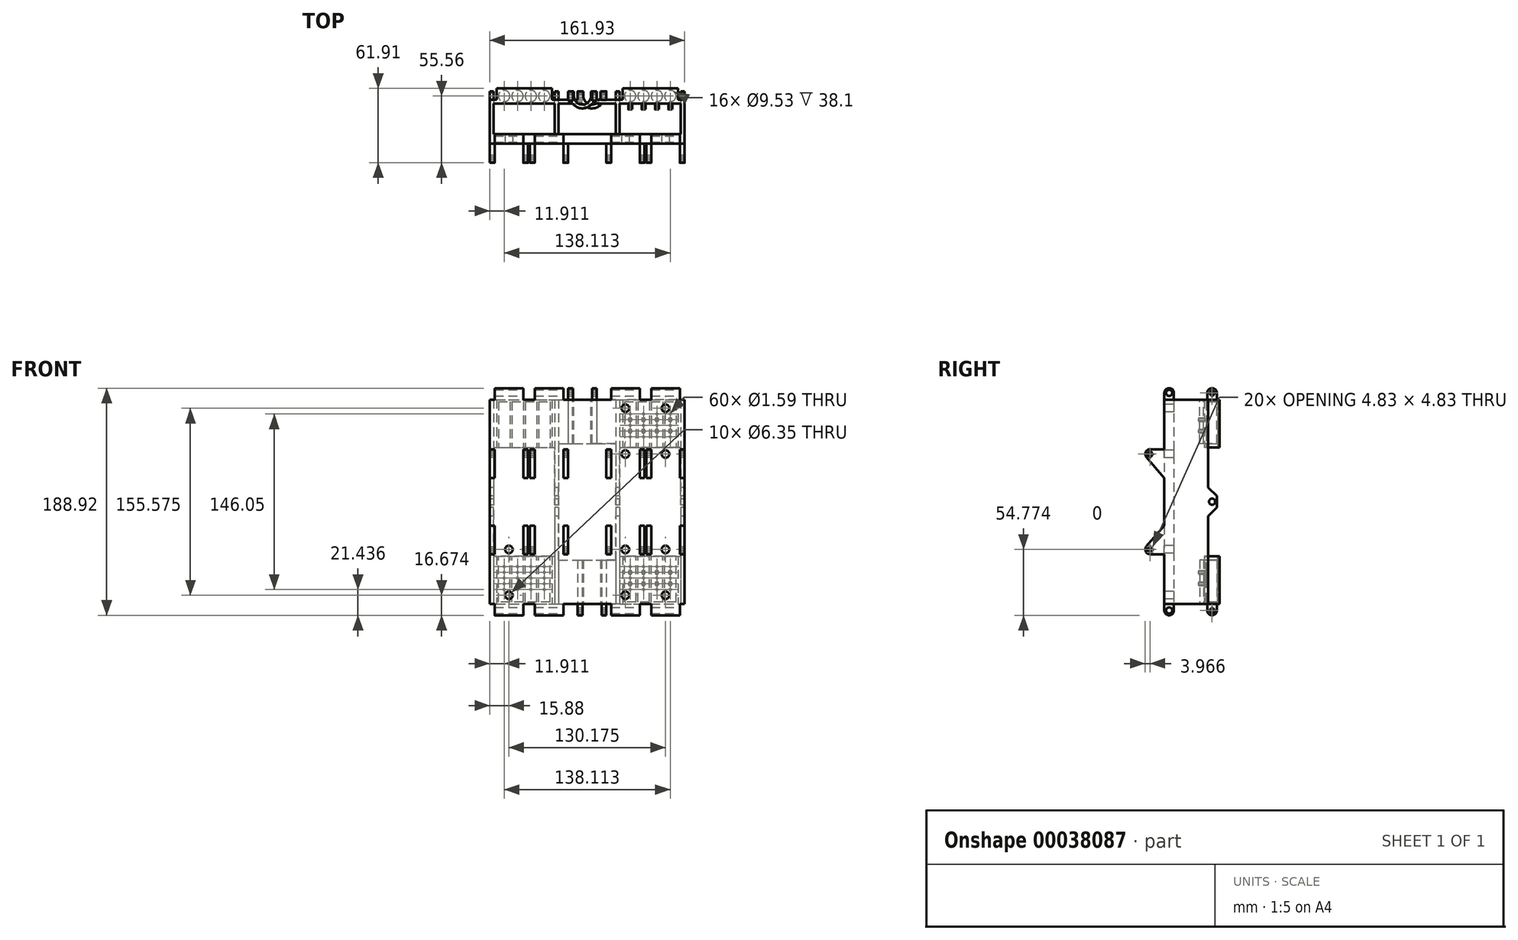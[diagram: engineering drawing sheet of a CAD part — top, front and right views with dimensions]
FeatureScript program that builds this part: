
annotation { "Feature Type Name" : "Feature", "Feature Type Description" : "" }
export const myFeature = defineFeature(function(context is Context, id is Id, definition is map)
    precondition{}
    {
        {
            var Q0;
            Q0=qCreatedBy(makeId("Top.planeOp"),FACE);
            var sketch = newSketch(context, id + "F0", { "sketchPlane" : qUnion([Q0])});
            skLineSegment(sketch, "E0.top", {"start": v(-3.18, -7.94) * mm, "end": v(158.75, -7.94) * mm});
            skLineSegment(sketch, "E1.left", {"start": v(0, 0) * mm, "end": v(0, 25.4) * mm});
            skLineSegment(sketch, "E1.right", {"start": v(-3.18, -7.94) * mm, "end": v(-3.17, 28.58) * mm});
            skLineSegment(sketch, "E2", {"start": v(0, 12.7) * mm, "end": v(-3.18, 12.7) * mm, "construction": true});
            skLineSegment(sketch, "E3", {"start": v(0, 0) * mm, "end": v(0, -7.94) * mm, "construction": true});
            skLineSegment(sketch, "E4.top", {"start": v(2.38, 38.1) * mm, "end": v(48.42, 38.1) * mm});
            skLineSegment(sketch, "E5.right", {"start": v(48.42, 28.57) * mm, "end": v(48.42, 38.1) * mm});
            skLineSegment(sketch, "E6", {"start": v(48.42, 28.57) * mm, "end": v(69.85, 28.57) * mm});
            skLineSegment(sketch, "E7.top", {"start": v(69.85, 35.72) * mm, "end": v(93.66, 35.72) * mm});
            skLineSegment(sketch, "E7.left", {"start": v(69.85, 28.57) * mm, "end": v(69.85, 35.72) * mm});
            skLineSegment(sketch, "E7.right", {"start": v(93.66, 28.57) * mm, "end": v(93.66, 35.72) * mm});
            skLineSegment(sketch, "E8.left", {"start": v(107.16, 28.57) * mm, "end": v(107.16, 38.1) * mm});
            skLineSegment(sketch, "E9", {"start": v(93.66, 28.57) * mm, "end": v(107.16, 28.57) * mm});
            skLineSegment(sketch, "E10.top", {"start": v(107.16, 38.1) * mm, "end": v(153.2, 38.1) * mm});
            skLineSegment(sketch, "E11", {"start": v(158.75, 28.57) * mm, "end": v(158.75, -7.94) * mm});
            skLineSegment(sketch, "E12", {"start": v(155.58, 25.4) * mm, "end": v(155.58, 0) * mm});
            skLineSegment(sketch, "E13", {"start": v(155.58, 12.7) * mm, "end": v(158.75, 12.7) * mm, "construction": true});
            skLineSegment(sketch, "E14", {"start": v(2.38, 38.1) * mm, "end": v(2.38, 28.57) * mm});
            skLineSegment(sketch, "E15", {"start": v(2.38, 28.58) * mm, "end": v(-3.18, 28.58) * mm});
            skLineSegment(sketch, "E16", {"start": v(153.2, 38.1) * mm, "end": v(153.2, 28.57) * mm});
            skLineSegment(sketch, "E17", {"start": v(153.2, 28.57) * mm, "end": v(158.75, 28.57) * mm});
            skLineSegment(sketch, "E18", {"start": v(0, 25.4) * mm, "end": v(50.8, 25.4) * mm});
            skLineSegment(sketch, "E19", {"start": v(0, 0) * mm, "end": v(50.8, 0) * mm});
            skLineSegment(sketch, "E20.bottom", {"start": v(50.8, 25.4) * mm, "end": v(53.98, 25.4) * mm, "construction": true});
            skLineSegment(sketch, "E20.top", {"start": v(50.8, 0) * mm, "end": v(53.98, 0) * mm, "construction": true});
            skLineSegment(sketch, "E20.left", {"start": v(50.8, 25.4) * mm, "end": v(50.8, 0) * mm});
            skLineSegment(sketch, "E20.right", {"start": v(53.98, 25.4) * mm, "end": v(53.98, 0) * mm});
            skLineSegment(sketch, "E21", {"start": v(53.98, 0) * mm, "end": v(101.6, 0) * mm});
            skLineSegment(sketch, "E22.bottom", {"start": v(101.6, 25.4) * mm, "end": v(104.78, 25.4) * mm, "construction": true});
            skLineSegment(sketch, "E22.top", {"start": v(101.6, 0) * mm, "end": v(104.78, 0) * mm, "construction": true});
            skLineSegment(sketch, "E22.left", {"start": v(101.6, 25.4) * mm, "end": v(101.6, 0) * mm});
            skLineSegment(sketch, "E22.right", {"start": v(104.78, 25.4) * mm, "end": v(104.78, 0) * mm});
            skLineSegment(sketch, "E23", {"start": v(104.78, 25.4) * mm, "end": v(155.58, 25.4) * mm});
            skLineSegment(sketch, "E24", {"start": v(104.78, 0) * mm, "end": v(155.58, 0) * mm});
            skLineSegment(sketch, "E25", {"start": v(0, 12.7) * mm, "end": v(25.4, 12.7) * mm, "construction": true});
            skLineSegment(sketch, "E26", {"start": v(25.4, 12.7) * mm, "end": v(25.4, 38.1) * mm, "construction": true});
            skLineSegment(sketch, "E27", {"start": v(155.58, 12.7) * mm, "end": v(104.78, 12.7) * mm, "construction": true});
            skLineSegment(sketch, "E28", {"start": v(53.98, 25.4) * mm, "end": v(69.85, 25.4) * mm});
            skLineSegment(sketch, "E29", {"start": v(101.6, 25.4) * mm, "end": v(93.66, 25.4) * mm});
            skLineSegment(sketch, "E30.top", {"start": v(69.85, 11.68) * mm, "end": v(93.66, 11.68) * mm});
            skLineSegment(sketch, "E30.left", {"start": v(69.85, 25.4) * mm, "end": v(69.85, 11.68) * mm});
            skLineSegment(sketch, "E30.right", {"start": v(93.66, 25.4) * mm, "end": v(93.66, 11.68) * mm});
            skLineSegment(sketch, "E31", {"start": v(25.4, 12.7) * mm, "end": v(50.8, 12.7) * mm, "construction": true});
            skLineSegment(sketch, "E32", {"start": v(81.76, 11.68) * mm, "end": v(81.76, 5.84) * mm, "construction": true});
            skLineSegment(sketch, "E33", {"start": v(81.76, 5.84) * mm, "end": v(77.79, 5.84) * mm, "construction": true});
            skLineSegment(sketch, "E34", {"start": v(77.79, 5.84) * mm, "end": v(77.79, 0) * mm, "construction": true});
            skSolve(sketch);
        }
        {
            var Q0;
            Q0 = qSketchRegion(id + "F0", true);
            extrude(context, id + "F1", {"entities" : qUnion([Q0]), "depth" : 39.69 * mm});
        }
        {
            var Q0;
            Q0=makeQuery(id+"F1.opExtrude","CAP_FACE",FACE,{"disambiguationData":[OSD([sQuery(id+"F0.wireOp",EDGE,"E0.bottom"),sQuery(id+"F0.wireOp",EDGE,"E0.top"),sQuery(id+"F0.wireOp",EDGE,"E1.left"),sQuery(id+"F0.wireOp",EDGE,"E1.right"),sQuery(id+"F0.wireOp",EDGE,"bac8c0be-aa32-425a-b017-748413468dc6.bottom"),sQuery(id+"F0.wireOp",EDGE,"bac8c0be-aa32-425a-b017-748413468dc6.top"),sQuery(id+"F0.wireOp",EDGE,"E4.top"),sQuery(id+"F0.wireOp",EDGE,"E4.left"),sQuery(id+"F0.wireOp",EDGE,"E4.right"),sQuery(id+"F0.wireOp",EDGE,"gwyJfFow-sQTI-wKbx-ZTm2-twAAZkwdv3cN"),sQuery(id+"F0.wireOp",EDGE,"E5.top"),sQuery(id+"F0.wireOp",EDGE,"E5.left"),sQuery(id+"F0.wireOp",EDGE,"E5.right"),sQuery(id+"F0.wireOp",EDGE,"E6"),sQuery(id+"F0.wireOp",EDGE,"E7.top"),sQuery(id+"F0.wireOp",EDGE,"E7.left"),sQuery(id+"F0.wireOp",EDGE,"E7.right"),sQuery(id+"F0.wireOp",EDGE,"E8.top"),sQuery(id+"F0.wireOp",EDGE,"E8.left"),sQuery(id+"F0.wireOp",EDGE,"E8.right"),sQuery(id+"F0.wireOp",EDGE,"E9"),sQuery(id+"F0.wireOp",EDGE,"IWzM8SZK-Yzhc-Plhi-QPJh-lKvNlgQkg0PU"),sQuery(id+"F0.wireOp",EDGE,"E10.top"),sQuery(id+"F0.wireOp",EDGE,"E10.left"),sQuery(id+"F0.wireOp",EDGE,"E10.right"),sQuery(id+"F0.wireOp",EDGE,"S0h3Bsn6-nd1q-4MY8-0u3a-wp1ZSmnOwf19"),sQuery(id+"F0.wireOp",EDGE,"E11"),sQuery(id+"F0.wireOp",EDGE,"E12")])],"isStart":false});
            var sketch = newSketch(context, id + "F2", { "sketchPlane" : qUnion([Q0])});
            skLineSegment(sketch, "E35", {"start": v(146.84, 31.75) * mm, "end": v(135.73, 31.75) * mm, "construction": true});
            skCircle(sketch, "E36", {"center": v(146.84, 31.75) * mm, "radius": 4.76 * mm});
            skCircle(sketch, "E37", {"center": v(135.73, 31.75) * mm, "radius": 4.76 * mm});
            skLineSegment(sketch, "E38", {"start": v(146.84, 31.75) * mm, "end": v(153.2, 31.75) * mm, "construction": true});
            skLineSegment(sketch, "E39", {"start": v(146.84, 31.75) * mm, "end": v(146.84, 38.1) * mm, "construction": true});
            skLineSegment(sketch, "E40", {"start": v(135.73, 31.75) * mm, "end": v(124.62, 31.75) * mm, "construction": true});
            skLineSegment(sketch, "E41", {"start": v(124.62, 31.75) * mm, "end": v(113.5, 31.75) * mm, "construction": true});
            skCircle(sketch, "E42", {"center": v(113.5, 31.75) * mm, "radius": 4.76 * mm});
            skCircle(sketch, "E43", {"center": v(124.62, 31.75) * mm, "radius": 4.76 * mm});
            skLineSegment(sketch, "E44", {"start": v(2.38, 31.75) * mm, "end": v(8.73, 31.75) * mm, "construction": true});
            skLineSegment(sketch, "E45", {"start": v(8.73, 31.75) * mm, "end": v(8.73, 38.1) * mm, "construction": true});
            skLineSegment(sketch, "E46", {"start": v(8.73, 31.75) * mm, "end": v(19.84, 31.75) * mm, "construction": true});
            skLineSegment(sketch, "E47", {"start": v(19.84, 31.75) * mm, "end": v(30.96, 31.75) * mm, "construction": true});
            skLineSegment(sketch, "E48", {"start": v(30.96, 31.75) * mm, "end": v(42.07, 31.75) * mm, "construction": true});
            skCircle(sketch, "E49", {"center": v(8.73, 31.75) * mm, "radius": 4.76 * mm});
            skCircle(sketch, "E50", {"center": v(19.84, 31.75) * mm, "radius": 4.76 * mm});
            skCircle(sketch, "E51", {"center": v(30.96, 31.75) * mm, "radius": 4.76 * mm});
            skCircle(sketch, "E52", {"center": v(42.07, 31.75) * mm, "radius": 4.76 * mm});
            skSolve(sketch);
        }
        {
            var Q0;
            Q0 = qSketchRegion(id + "F2", true);
            extrude(context, id + "F3", {"entities" : qUnion([Q0]), "operationType" : NewBodyOperationType.REMOVE, "oppositeDirection" : true, "depth" : 38.1 * mm});
        }
        {
            var Q0;
            Q0=makeQuery(id+"F1.opExtrude","CAP_FACE",FACE,{"disambiguationData":[OSD([sQuery(id+"F0.wireOp",EDGE,"E0.bottom"),sQuery(id+"F0.wireOp",EDGE,"E0.top"),sQuery(id+"F0.wireOp",EDGE,"E1.left"),sQuery(id+"F0.wireOp",EDGE,"E1.right"),sQuery(id+"F0.wireOp",EDGE,"bac8c0be-aa32-425a-b017-748413468dc6.bottom"),sQuery(id+"F0.wireOp",EDGE,"bac8c0be-aa32-425a-b017-748413468dc6.top"),sQuery(id+"F0.wireOp",EDGE,"E4.top"),sQuery(id+"F0.wireOp",EDGE,"E4.left"),sQuery(id+"F0.wireOp",EDGE,"E4.right"),sQuery(id+"F0.wireOp",EDGE,"gwyJfFow-sQTI-wKbx-ZTm2-twAAZkwdv3cN"),sQuery(id+"F0.wireOp",EDGE,"E5.top"),sQuery(id+"F0.wireOp",EDGE,"E5.left"),sQuery(id+"F0.wireOp",EDGE,"E5.right"),sQuery(id+"F0.wireOp",EDGE,"E6"),sQuery(id+"F0.wireOp",EDGE,"E7.top"),sQuery(id+"F0.wireOp",EDGE,"E7.left"),sQuery(id+"F0.wireOp",EDGE,"E7.right"),sQuery(id+"F0.wireOp",EDGE,"E8.top"),sQuery(id+"F0.wireOp",EDGE,"E8.left"),sQuery(id+"F0.wireOp",EDGE,"E8.right"),sQuery(id+"F0.wireOp",EDGE,"E9"),sQuery(id+"F0.wireOp",EDGE,"IWzM8SZK-Yzhc-Plhi-QPJh-lKvNlgQkg0PU"),sQuery(id+"F0.wireOp",EDGE,"E10.top"),sQuery(id+"F0.wireOp",EDGE,"E10.left"),sQuery(id+"F0.wireOp",EDGE,"E10.right"),sQuery(id+"F0.wireOp",EDGE,"S0h3Bsn6-nd1q-4MY8-0u3a-wp1ZSmnOwf19"),sQuery(id+"F0.wireOp",EDGE,"E11"),sQuery(id+"F0.wireOp",EDGE,"E12")])],"isStart":true});
            var sketch = newSketch(context, id + "F4", { "sketchPlane" : qUnion([Q0])});
            skLineSegment(sketch, "E53.bottom", {"start": v(88.9, -35.72) * mm, "end": v(74.61, -35.72) * mm});
            skLineSegment(sketch, "E53.top", {"start": v(88.9, -31.75) * mm, "end": v(74.61, -31.75) * mm, "construction": true});
            skLineSegment(sketch, "E53.left", {"start": v(88.9, -35.72) * mm, "end": v(88.9, -31.75) * mm});
            skLineSegment(sketch, "E53.right", {"start": v(74.61, -35.72) * mm, "end": v(74.61, -31.75) * mm});
            skArc(sketch, "E54", {"start": v(88.9, -31.75) * mm, "mid": v(81.76, -24.6) * mm, "end": v(74.61, -31.75) * mm});
            skPoint(sketch, "E55", {"position": v(81.76, -35.72) * mm});
            skLineSegment(sketch, "E56", {"start": v(93.66, -25.4) * mm, "end": v(89.89, -25.4) * mm});
            skLineSegment(sketch, "E57", {"start": v(69.85, -25.4) * mm, "end": v(73.62, -25.4) * mm});
            skLineSegment(sketch, "E58", {"start": v(81.76, -24.6) * mm, "end": v(81.76, -21.43) * mm, "construction": true});
            skArc(sketch, "E59", {"start": v(89.89, -25.4) * mm, "mid": v(81.76, -21.43) * mm, "end": v(73.62, -25.4) * mm});
            skLineSegment(sketch, "E60.bottom", {"start": v(93.66, -11.68) * mm, "end": v(69.85, -11.68) * mm});
            skLineSegment(sketch, "E60.left", {"start": v(93.66, -11.68) * mm, "end": v(93.66, -25.4) * mm});
            skLineSegment(sketch, "E60.right", {"start": v(69.85, -11.68) * mm, "end": v(69.85, -25.4) * mm});
            skSolve(sketch);
        }
        {
            var Q0;
            Q0 = qSketchRegion(id + "F4", true);
            var Q1;
            Q1=makeQuery(id+"F1.opExtrude","CAP_FACE",FACE,{"disambiguationData":[OSD([sQuery(id+"F0.wireOp",EDGE,"E0.bottom"),sQuery(id+"F0.wireOp",EDGE,"E0.top"),sQuery(id+"F0.wireOp",EDGE,"E1.left"),sQuery(id+"F0.wireOp",EDGE,"E1.right"),sQuery(id+"F0.wireOp",EDGE,"bac8c0be-aa32-425a-b017-748413468dc6.bottom"),sQuery(id+"F0.wireOp",EDGE,"bac8c0be-aa32-425a-b017-748413468dc6.top"),sQuery(id+"F0.wireOp",EDGE,"E4.top"),sQuery(id+"F0.wireOp",EDGE,"E4.left"),sQuery(id+"F0.wireOp",EDGE,"E4.right"),sQuery(id+"F0.wireOp",EDGE,"gwyJfFow-sQTI-wKbx-ZTm2-twAAZkwdv3cN"),sQuery(id+"F0.wireOp",EDGE,"E5.top"),sQuery(id+"F0.wireOp",EDGE,"E5.left"),sQuery(id+"F0.wireOp",EDGE,"E5.right"),sQuery(id+"F0.wireOp",EDGE,"E6"),sQuery(id+"F0.wireOp",EDGE,"E7.top"),sQuery(id+"F0.wireOp",EDGE,"E7.left"),sQuery(id+"F0.wireOp",EDGE,"E7.right"),sQuery(id+"F0.wireOp",EDGE,"E8.top"),sQuery(id+"F0.wireOp",EDGE,"E8.left"),sQuery(id+"F0.wireOp",EDGE,"E8.right"),sQuery(id+"F0.wireOp",EDGE,"E9"),sQuery(id+"F0.wireOp",EDGE,"IWzM8SZK-Yzhc-Plhi-QPJh-lKvNlgQkg0PU"),sQuery(id+"F0.wireOp",EDGE,"E10.top"),sQuery(id+"F0.wireOp",EDGE,"E10.left"),sQuery(id+"F0.wireOp",EDGE,"E10.right"),sQuery(id+"F0.wireOp",EDGE,"S0h3Bsn6-nd1q-4MY8-0u3a-wp1ZSmnOwf19"),sQuery(id+"F0.wireOp",EDGE,"E11"),sQuery(id+"F0.wireOp",EDGE,"E12")])],"isStart":false});
            extrude(context, id + "F5", {"entities" : qUnion([Q0]), "operationType" : NewBodyOperationType.REMOVE, "endBound" : BoundingType.UP_TO_SURFACE, "oppositeDirection" : true, "endBoundEntityFace" : qUnion([Q1]), "depth" : 25.4 * mm});
        }
        {
            var Q0;
            Q0=makeQuery(id+"F1.opExtrude","CAP_FACE",FACE,{"disambiguationData":[OSD([sQuery(id+"F0.wireOp",EDGE,"E0.bottom"),sQuery(id+"F0.wireOp",EDGE,"E0.top"),sQuery(id+"F0.wireOp",EDGE,"E1.left"),sQuery(id+"F0.wireOp",EDGE,"E1.right"),sQuery(id+"F0.wireOp",EDGE,"bac8c0be-aa32-425a-b017-748413468dc6.bottom"),sQuery(id+"F0.wireOp",EDGE,"bac8c0be-aa32-425a-b017-748413468dc6.top"),sQuery(id+"F0.wireOp",EDGE,"E4.top"),sQuery(id+"F0.wireOp",EDGE,"E4.left"),sQuery(id+"F0.wireOp",EDGE,"E4.right"),sQuery(id+"F0.wireOp",EDGE,"gwyJfFow-sQTI-wKbx-ZTm2-twAAZkwdv3cN"),sQuery(id+"F0.wireOp",EDGE,"E5.top"),sQuery(id+"F0.wireOp",EDGE,"E5.left"),sQuery(id+"F0.wireOp",EDGE,"E5.right"),sQuery(id+"F0.wireOp",EDGE,"E6"),sQuery(id+"F0.wireOp",EDGE,"E7.top"),sQuery(id+"F0.wireOp",EDGE,"E7.left"),sQuery(id+"F0.wireOp",EDGE,"E7.right"),sQuery(id+"F0.wireOp",EDGE,"E8.top"),sQuery(id+"F0.wireOp",EDGE,"E8.left"),sQuery(id+"F0.wireOp",EDGE,"E8.right"),sQuery(id+"F0.wireOp",EDGE,"E9"),sQuery(id+"F0.wireOp",EDGE,"IWzM8SZK-Yzhc-Plhi-QPJh-lKvNlgQkg0PU"),sQuery(id+"F0.wireOp",EDGE,"E10.top"),sQuery(id+"F0.wireOp",EDGE,"E10.left"),sQuery(id+"F0.wireOp",EDGE,"E10.right"),sQuery(id+"F0.wireOp",EDGE,"S0h3Bsn6-nd1q-4MY8-0u3a-wp1ZSmnOwf19"),sQuery(id+"F0.wireOp",EDGE,"E11"),sQuery(id+"F0.wireOp",EDGE,"E12")])],"isStart":true});
            var sketch = newSketch(context, id + "F6", { "sketchPlane" : qUnion([Q0])});
            skLineSegment(sketch, "E61.bottom", {"start": v(93.66, -35.72) * mm, "end": v(89.7, -35.72) * mm});
            skLineSegment(sketch, "E61.top", {"start": v(93.66, -27.78) * mm, "end": v(89.7, -27.78) * mm});
            skLineSegment(sketch, "E61.left", {"start": v(93.66, -35.72) * mm, "end": v(93.66, -27.78) * mm});
            skLineSegment(sketch, "E61.right", {"start": v(89.7, -35.72) * mm, "end": v(89.7, -27.78) * mm});
            skLineSegment(sketch, "E62.bottom", {"start": v(69.85, -35.72) * mm, "end": v(73.82, -35.72) * mm});
            skLineSegment(sketch, "E62.top", {"start": v(69.85, -27.78) * mm, "end": v(73.82, -27.78) * mm});
            skLineSegment(sketch, "E62.left", {"start": v(69.85, -35.72) * mm, "end": v(69.85, -27.78) * mm});
            skLineSegment(sketch, "E62.right", {"start": v(73.82, -35.72) * mm, "end": v(73.82, -27.78) * mm});
            skSolve(sketch);
        }
        {
            var Q0;
            Q0 = qSketchRegion(id + "F6", true);
            extrude(context, id + "F7", {"entities" : qUnion([Q0]), "operationType" : NewBodyOperationType.ADD, "depth" : 9.52 * mm});
        }
        {
            var Q0;
            Q0=makeQuery(id+"F1.opExtrude","CAP_FACE",FACE,{"disambiguationData":[OSD([sQuery(id+"F0.wireOp",EDGE,"E0.bottom"),sQuery(id+"F0.wireOp",EDGE,"E0.top"),sQuery(id+"F0.wireOp",EDGE,"E1.left"),sQuery(id+"F0.wireOp",EDGE,"E1.right"),sQuery(id+"F0.wireOp",EDGE,"bac8c0be-aa32-425a-b017-748413468dc6.bottom"),sQuery(id+"F0.wireOp",EDGE,"bac8c0be-aa32-425a-b017-748413468dc6.top"),sQuery(id+"F0.wireOp",EDGE,"E4.top"),sQuery(id+"F0.wireOp",EDGE,"E4.left"),sQuery(id+"F0.wireOp",EDGE,"E4.right"),sQuery(id+"F0.wireOp",EDGE,"gwyJfFow-sQTI-wKbx-ZTm2-twAAZkwdv3cN"),sQuery(id+"F0.wireOp",EDGE,"E5.top"),sQuery(id+"F0.wireOp",EDGE,"E5.left"),sQuery(id+"F0.wireOp",EDGE,"E5.right"),sQuery(id+"F0.wireOp",EDGE,"E6"),sQuery(id+"F0.wireOp",EDGE,"E7.top"),sQuery(id+"F0.wireOp",EDGE,"E7.left"),sQuery(id+"F0.wireOp",EDGE,"E7.right"),sQuery(id+"F0.wireOp",EDGE,"E8.top"),sQuery(id+"F0.wireOp",EDGE,"E8.left"),sQuery(id+"F0.wireOp",EDGE,"E8.right"),sQuery(id+"F0.wireOp",EDGE,"E9"),sQuery(id+"F0.wireOp",EDGE,"IWzM8SZK-Yzhc-Plhi-QPJh-lKvNlgQkg0PU"),sQuery(id+"F0.wireOp",EDGE,"E10.top"),sQuery(id+"F0.wireOp",EDGE,"E10.left"),sQuery(id+"F0.wireOp",EDGE,"E10.right"),sQuery(id+"F0.wireOp",EDGE,"S0h3Bsn6-nd1q-4MY8-0u3a-wp1ZSmnOwf19"),sQuery(id+"F0.wireOp",EDGE,"E11"),sQuery(id+"F0.wireOp",EDGE,"E12")])],"isStart":true});
            var sketch = newSketch(context, id + "F8", { "sketchPlane" : qUnion([Q0])});
            skLineSegment(sketch, "E63.bottom", {"start": v(154.78, 0) * mm, "end": v(130.97, 0) * mm});
            skLineSegment(sketch, "E63.top", {"start": v(154.78, 7.94) * mm, "end": v(130.97, 7.94) * mm});
            skLineSegment(sketch, "E63.left", {"start": v(154.78, 0) * mm, "end": v(154.78, 7.94) * mm});
            skLineSegment(sketch, "E63.right", {"start": v(130.97, 0) * mm, "end": v(130.97, 7.94) * mm});
            skLineSegment(sketch, "E64.bottom", {"start": v(0.8, 7.94) * mm, "end": v(24.6, 7.94) * mm});
            skLineSegment(sketch, "E64.top", {"start": v(0.8, 0) * mm, "end": v(24.6, 0) * mm});
            skLineSegment(sketch, "E64.left", {"start": v(0.8, 7.94) * mm, "end": v(0.8, 0) * mm});
            skLineSegment(sketch, "E64.right", {"start": v(24.6, 7.94) * mm, "end": v(24.6, 0) * mm});
            skLineSegment(sketch, "E65", {"start": v(0.8, 3.97) * mm, "end": v(-3.18, 3.97) * mm, "construction": true});
            skLineSegment(sketch, "E66", {"start": v(154.78, 3.97) * mm, "end": v(158.75, 3.97) * mm, "construction": true});
            skLineSegment(sketch, "E67", {"start": v(130.97, 3.97) * mm, "end": v(121.44, 3.97) * mm, "construction": true});
            skLineSegment(sketch, "E68", {"start": v(24.6, 3.97) * mm, "end": v(34.13, 3.97) * mm, "construction": true});
            skLineSegment(sketch, "E69.bottom", {"start": v(121.44, 0) * mm, "end": v(97.63, 0) * mm});
            skLineSegment(sketch, "E69.top", {"start": v(121.44, 7.94) * mm, "end": v(97.63, 7.94) * mm});
            skLineSegment(sketch, "E69.left", {"start": v(121.44, 0) * mm, "end": v(121.44, 7.94) * mm});
            skLineSegment(sketch, "E69.right", {"start": v(97.63, 0) * mm, "end": v(97.63, 7.94) * mm});
            skLineSegment(sketch, "E70.bottom", {"start": v(34.13, 0) * mm, "end": v(57.94, 0) * mm});
            skLineSegment(sketch, "E70.top", {"start": v(34.13, 7.94) * mm, "end": v(57.94, 7.94) * mm});
            skLineSegment(sketch, "E70.left", {"start": v(34.13, 0) * mm, "end": v(34.13, 7.94) * mm});
            skLineSegment(sketch, "E70.right", {"start": v(57.94, 0) * mm, "end": v(57.94, 7.94) * mm});
            skPoint(sketch, "E71", {"position": v(142.88, 0) * mm});
            skSolve(sketch);
        }
        {
            var Q0;
            Q0 = qSketchRegion(id + "F8", true);
            extrude(context, id + "F9", {"entities" : qUnion([Q0]), "operationType" : NewBodyOperationType.ADD, "depth" : 9.52 * mm});
        }
        {
            var Q0;
            Q0=makeQuery(id+"F1.opExtrude","CAP_FACE",FACE,{"disambiguationData":[OSD([sQuery(id+"F0.wireOp",EDGE,"E0.bottom"),sQuery(id+"F0.wireOp",EDGE,"E0.top"),sQuery(id+"F0.wireOp",EDGE,"E1.left"),sQuery(id+"F0.wireOp",EDGE,"E1.right"),sQuery(id+"F0.wireOp",EDGE,"bac8c0be-aa32-425a-b017-748413468dc6.bottom"),sQuery(id+"F0.wireOp",EDGE,"bac8c0be-aa32-425a-b017-748413468dc6.top"),sQuery(id+"F0.wireOp",EDGE,"E4.top"),sQuery(id+"F0.wireOp",EDGE,"E4.left"),sQuery(id+"F0.wireOp",EDGE,"E4.right"),sQuery(id+"F0.wireOp",EDGE,"gwyJfFow-sQTI-wKbx-ZTm2-twAAZkwdv3cN"),sQuery(id+"F0.wireOp",EDGE,"E5.top"),sQuery(id+"F0.wireOp",EDGE,"E5.left"),sQuery(id+"F0.wireOp",EDGE,"E5.right"),sQuery(id+"F0.wireOp",EDGE,"E6"),sQuery(id+"F0.wireOp",EDGE,"E7.top"),sQuery(id+"F0.wireOp",EDGE,"E7.left"),sQuery(id+"F0.wireOp",EDGE,"E7.right"),sQuery(id+"F0.wireOp",EDGE,"E8.top"),sQuery(id+"F0.wireOp",EDGE,"E8.left"),sQuery(id+"F0.wireOp",EDGE,"E8.right"),sQuery(id+"F0.wireOp",EDGE,"E9"),sQuery(id+"F0.wireOp",EDGE,"IWzM8SZK-Yzhc-Plhi-QPJh-lKvNlgQkg0PU"),sQuery(id+"F0.wireOp",EDGE,"E10.top"),sQuery(id+"F0.wireOp",EDGE,"E10.left"),sQuery(id+"F0.wireOp",EDGE,"E10.right"),sQuery(id+"F0.wireOp",EDGE,"S0h3Bsn6-nd1q-4MY8-0u3a-wp1ZSmnOwf19"),sQuery(id+"F0.wireOp",EDGE,"E11"),sQuery(id+"F0.wireOp",EDGE,"E12")])],"isStart":false});
            var sketch = newSketch(context, id + "F10", { "sketchPlane" : qUnion([Q0])});
            skLineSegment(sketch, "E72.bottom", {"start": v(0, 35.72) * mm, "end": v(-3.18, 35.72) * mm});
            skLineSegment(sketch, "E72.top", {"start": v(158.75, -7.94) * mm, "end": v(-3.18, -7.94) * mm});
            skLineSegment(sketch, "E72.right", {"start": v(-3.17, 35.72) * mm, "end": v(-3.17, -7.94) * mm});
            skLineSegment(sketch, "E73.bottom", {"start": v(155.58, 35.72) * mm, "end": v(158.75, 35.72) * mm});
            skLineSegment(sketch, "E73.left", {"start": v(155.58, 35.72) * mm, "end": v(155.58, 0) * mm});
            skLineSegment(sketch, "E73.right", {"start": v(158.75, 35.72) * mm, "end": v(158.75, -7.94) * mm});
            skLineSegment(sketch, "E74.left", {"start": v(0, 35.72) * mm, "end": v(0, 0) * mm});
            skLineSegment(sketch, "E75", {"start": v(146.84, 31.75) * mm, "end": v(151.2, 31.75) * mm, "construction": true});
            skLineSegment(sketch, "E76", {"start": v(151.2, 31.75) * mm, "end": v(151.2, 35.72) * mm, "construction": true});
            skLineSegment(sketch, "E77", {"start": v(151.2, 35.72) * mm, "end": v(155.58, 35.72) * mm, "construction": true});
            skLineSegment(sketch, "E78.bottom", {"start": v(50.8, 0) * mm, "end": v(53.98, 0) * mm, "construction": true});
            skLineSegment(sketch, "E78.top", {"start": v(50.8, 35.72) * mm, "end": v(53.98, 35.72) * mm});
            skLineSegment(sketch, "E78.left", {"start": v(50.8, 0) * mm, "end": v(50.8, 35.72) * mm});
            skLineSegment(sketch, "E78.right", {"start": v(53.98, 0) * mm, "end": v(53.98, 35.72) * mm});
            skLineSegment(sketch, "E79.bottom", {"start": v(104.78, 0) * mm, "end": v(101.6, 0) * mm, "construction": true});
            skLineSegment(sketch, "E79.top", {"start": v(104.78, 35.72) * mm, "end": v(101.6, 35.72) * mm});
            skLineSegment(sketch, "E79.left", {"start": v(104.78, 0) * mm, "end": v(104.78, 35.72) * mm});
            skLineSegment(sketch, "E79.right", {"start": v(101.6, 0) * mm, "end": v(101.6, 35.72) * mm});
            skLineSegment(sketch, "E80", {"start": v(104.78, 0) * mm, "end": v(155.58, 0) * mm});
            skLineSegment(sketch, "E81", {"start": v(0, 0) * mm, "end": v(50.8, 0) * mm});
            skLineSegment(sketch, "E82", {"start": v(53.98, 0) * mm, "end": v(101.6, 0) * mm});
            skSolve(sketch);
        }
        {
            var Q0;
            Q0 = qSketchRegion(id + "F10", true);
            extrude(context, id + "F11", {"entities" : qUnion([Q0]), "operationType" : NewBodyOperationType.ADD, "depth" : 90.49 * mm});
        }
        {
            var Q0;
            Q0=makeQuery(id+"F11.opExtrude","CAP_FACE",FACE,{"disambiguationData":[OSD([sQuery(id+"F10.wireOp",EDGE,"E72.bottom"),sQuery(id+"F10.wireOp",EDGE,"E72.top"),sQuery(id+"F10.wireOp",EDGE,"E72.right"),sQuery(id+"F10.wireOp",EDGE,"E73.bottom"),sQuery(id+"F10.wireOp",EDGE,"E73.left"),sQuery(id+"F10.wireOp",EDGE,"E73.right"),sQuery(id+"F10.wireOp",EDGE,"E74.left"),sQuery(id+"F10.wireOp",EDGE,"E78.top"),sQuery(id+"F10.wireOp",EDGE,"E78.left"),sQuery(id+"F10.wireOp",EDGE,"E78.right"),sQuery(id+"F10.wireOp",EDGE,"E79.top"),sQuery(id+"F10.wireOp",EDGE,"E79.left"),sQuery(id+"F10.wireOp",EDGE,"E79.right"),sQuery(id+"F10.wireOp",EDGE,"E80"),sQuery(id+"F10.wireOp",EDGE,"E81"),sQuery(id+"F10.wireOp",EDGE,"E82")])],"isStart":false});
            var sketch = newSketch(context, id + "F12", { "sketchPlane" : qUnion([Q0])});
            skLineSegment(sketch, "E83.top", {"start": v(-3.17, -7.94) * mm, "end": v(158.75, -7.94) * mm});
            skLineSegment(sketch, "E83.left", {"start": v(-3.17, 28.58) * mm, "end": v(-3.17, -7.94) * mm});
            skLineSegment(sketch, "E83.right", {"start": v(158.75, 28.57) * mm, "end": v(158.75, -7.94) * mm});
            skLineSegment(sketch, "E84", {"start": v(-3.17, 28.58) * mm, "end": v(2.38, 28.58) * mm});
            skLineSegment(sketch, "E85.top", {"start": v(2.38, 38.1) * mm, "end": v(48.42, 38.1) * mm});
            skLineSegment(sketch, "E85.left", {"start": v(2.38, 28.57) * mm, "end": v(2.38, 38.1) * mm});
            skLineSegment(sketch, "E85.right", {"start": v(48.42, 28.57) * mm, "end": v(48.42, 38.1) * mm});
            skLineSegment(sketch, "E86", {"start": v(48.42, 28.58) * mm, "end": v(61.91, 28.58) * mm});
            skLineSegment(sketch, "E87.bottom", {"start": v(0, 0) * mm, "end": v(50.8, 0) * mm});
            skLineSegment(sketch, "E87.top", {"start": v(0, 25.4) * mm, "end": v(50.8, 25.4) * mm});
            skLineSegment(sketch, "E87.left", {"start": v(0, 0) * mm, "end": v(0, 25.4) * mm});
            skLineSegment(sketch, "E87.right", {"start": v(50.8, 0) * mm, "end": v(50.8, 25.4) * mm});
            skLineSegment(sketch, "E88.bottom", {"start": v(53.97, 0) * mm, "end": v(101.6, 0) * mm});
            skLineSegment(sketch, "E88.left", {"start": v(53.98, 0) * mm, "end": v(53.98, 25.4) * mm});
            skLineSegment(sketch, "E88.right", {"start": v(101.6, 0) * mm, "end": v(101.6, 25.4) * mm});
            skLineSegment(sketch, "E89.bottom", {"start": v(104.78, 0) * mm, "end": v(155.58, 0) * mm});
            skLineSegment(sketch, "E89.top", {"start": v(104.78, 25.4) * mm, "end": v(155.58, 25.4) * mm});
            skLineSegment(sketch, "E89.left", {"start": v(104.78, 0) * mm, "end": v(104.78, 25.4) * mm});
            skLineSegment(sketch, "E89.right", {"start": v(155.58, 0) * mm, "end": v(155.58, 25.4) * mm});
            skLineSegment(sketch, "E90", {"start": v(53.98, 25.4) * mm, "end": v(61.91, 25.4) * mm});
            skLineSegment(sketch, "E91", {"start": v(101.6, 25.4) * mm, "end": v(85.72, 25.4) * mm});
            skLineSegment(sketch, "E92", {"start": v(158.75, 28.57) * mm, "end": v(153.2, 28.57) * mm});
            skLineSegment(sketch, "E93.bottom", {"start": v(61.91, 28.58) * mm, "end": v(85.72, 28.58) * mm, "construction": true});
            skLineSegment(sketch, "E93.top", {"start": v(61.91, 35.72) * mm, "end": v(85.72, 35.72) * mm});
            skLineSegment(sketch, "E93.left", {"start": v(61.91, 28.57) * mm, "end": v(61.91, 35.72) * mm});
            skLineSegment(sketch, "E93.right", {"start": v(85.72, 28.57) * mm, "end": v(85.72, 35.72) * mm});
            skLineSegment(sketch, "E94.bottom", {"start": v(153.2, 28.57) * mm, "end": v(107.16, 28.57) * mm, "construction": true});
            skLineSegment(sketch, "E94.top", {"start": v(153.2, 38.1) * mm, "end": v(107.16, 38.1) * mm});
            skLineSegment(sketch, "E94.left", {"start": v(153.2, 28.57) * mm, "end": v(153.2, 38.1) * mm});
            skLineSegment(sketch, "E94.right", {"start": v(107.16, 28.57) * mm, "end": v(107.16, 38.1) * mm});
            skLineSegment(sketch, "E95", {"start": v(77.79, 0) * mm, "end": v(77.79, 5.84) * mm, "construction": true});
            skLineSegment(sketch, "E96", {"start": v(73.82, 5.84) * mm, "end": v(77.79, 5.84) * mm, "construction": true});
            skLineSegment(sketch, "E97.bottom", {"start": v(61.91, 25.4) * mm, "end": v(85.72, 25.4) * mm, "construction": true});
            skLineSegment(sketch, "E97.top", {"start": v(61.91, 11.68) * mm, "end": v(85.72, 11.68) * mm});
            skLineSegment(sketch, "E97.left", {"start": v(61.91, 25.4) * mm, "end": v(61.91, 11.68) * mm});
            skLineSegment(sketch, "E97.right", {"start": v(85.72, 25.4) * mm, "end": v(85.72, 11.68) * mm});
            skLineSegment(sketch, "E98", {"start": v(73.82, 11.68) * mm, "end": v(73.82, 5.84) * mm, "construction": true});
            skLineSegment(sketch, "E99", {"start": v(85.72, 28.58) * mm, "end": v(107.16, 28.58) * mm});
            skLineSegment(sketch, "E100", {"start": v(73.82, 28.57) * mm, "end": v(73.82, 25.4) * mm, "construction": true});
            skSolve(sketch);
        }
        {
            var Q0;
            {var subQ5=sQuery(id+"F12.wireOp",EDGE,"E89.top");Q0=makeQuery(id+"F12.imprint","IMPRINT",FACE,{"disambiguationData":[TD([[makeQuery(id+"F12.imprint","IMPRINT",EDGE,{"derivedFrom":subQ5}),1.0]])]});}
            var Q1;
            {var subQ9=sQuery(id+"F12.wireOp",EDGE,"E90");Q1=makeQuery(id+"F12.imprint","IMPRINT",FACE,{"disambiguationData":[TD([[makeQuery(id+"F12.imprint","IMPRINT",EDGE,{"derivedFrom":subQ9}),1.0]])]});}
            var Q2;
            Q2=makeQuery(id+"F12.imprint","IMPRINT",FACE,{"disambiguationData":[TD([[makeQuery(id+"F12.imprint","IMPRINT",EDGE,{"derivedFrom":sQuery(id+"F12.wireOp",EDGE,"E83.top")}),1.0]])]});
            var Q3;
            {var subQ5=sQuery(id+"F12.wireOp",EDGE,"E85.top");Q3=makeQuery(id+"F12.imprint","IMPRINT",FACE,{"disambiguationData":[TD([[makeQuery(id+"F12.imprint","IMPRINT",EDGE,{"derivedFrom":subQ5}),-1.0]])]});}
            extrude(context, id + "F13", {"entities" : qUnion([Q0, Q1, Q2, Q3]), "operationType" : NewBodyOperationType.ADD, "depth" : 39.69 * mm});
        }
        {
            var Q0;
            Q0=makeQuery(id+"F13.opExtrude","CAP_FACE",FACE,{"disambiguationData":[OSD([sQuery(id+"F12.wireOp",EDGE,"E83.top"),sQuery(id+"F12.wireOp",EDGE,"E83.left"),sQuery(id+"F12.wireOp",EDGE,"E83.right"),sQuery(id+"F12.wireOp",EDGE,"E84"),sQuery(id+"F12.wireOp",EDGE,"E85.top"),sQuery(id+"F12.wireOp",EDGE,"E85.left"),sQuery(id+"F12.wireOp",EDGE,"E85.right"),sQuery(id+"F12.wireOp",EDGE,"E86"),sQuery(id+"F12.wireOp",EDGE,"E87.bottom"),sQuery(id+"F12.wireOp",EDGE,"E87.top"),sQuery(id+"F12.wireOp",EDGE,"E87.left"),sQuery(id+"F12.wireOp",EDGE,"E87.right"),sQuery(id+"F12.wireOp",EDGE,"E88.bottom"),sQuery(id+"F12.wireOp",EDGE,"E88.left"),sQuery(id+"F12.wireOp",EDGE,"E88.right"),sQuery(id+"F12.wireOp",EDGE,"E89.bottom"),sQuery(id+"F12.wireOp",EDGE,"E89.top"),sQuery(id+"F12.wireOp",EDGE,"E89.left"),sQuery(id+"F12.wireOp",EDGE,"E89.right"),sQuery(id+"F12.wireOp",EDGE,"E90"),sQuery(id+"F12.wireOp",EDGE,"E91"),sQuery(id+"F12.wireOp",EDGE,"E92"),sQuery(id+"F12.wireOp",EDGE,"E93.top"),sQuery(id+"F12.wireOp",EDGE,"E93.left"),sQuery(id+"F12.wireOp",EDGE,"E93.right"),sQuery(id+"F12.wireOp",EDGE,"E94.top"),sQuery(id+"F12.wireOp",EDGE,"E94.left"),sQuery(id+"F12.wireOp",EDGE,"E94.right"),sQuery(id+"F12.wireOp",EDGE,"E97.top"),sQuery(id+"F12.wireOp",EDGE,"E97.left"),sQuery(id+"F12.wireOp",EDGE,"E97.right"),sQuery(id+"F12.wireOp",EDGE,"E99")])],"isStart":false});
            var sketch = newSketch(context, id + "F14", { "sketchPlane" : qUnion([Q0])});
            skLineSegment(sketch, "E101.bottom", {"start": v(0.8, 0) * mm, "end": v(24.6, 0) * mm});
            skLineSegment(sketch, "E101.top", {"start": v(0.8, -7.94) * mm, "end": v(24.6, -7.94) * mm});
            skLineSegment(sketch, "E101.left", {"start": v(0.8, 0) * mm, "end": v(0.8, -7.94) * mm});
            skLineSegment(sketch, "E101.right", {"start": v(24.6, 0) * mm, "end": v(24.6, -7.94) * mm});
            skLineSegment(sketch, "E102.bottom", {"start": v(97.63, 0) * mm, "end": v(121.44, 0) * mm});
            skLineSegment(sketch, "E102.top", {"start": v(97.63, -7.94) * mm, "end": v(121.44, -7.94) * mm});
            skLineSegment(sketch, "E102.left", {"start": v(97.63, 0) * mm, "end": v(97.63, -7.94) * mm});
            skLineSegment(sketch, "E102.right", {"start": v(121.44, 0) * mm, "end": v(121.44, -7.94) * mm});
            skLineSegment(sketch, "E103.bottom", {"start": v(130.97, 0) * mm, "end": v(154.78, 0) * mm});
            skLineSegment(sketch, "E103.top", {"start": v(130.97, -7.94) * mm, "end": v(154.78, -7.94) * mm});
            skLineSegment(sketch, "E103.left", {"start": v(130.97, 0) * mm, "end": v(130.97, -7.94) * mm});
            skLineSegment(sketch, "E103.right", {"start": v(154.78, 0) * mm, "end": v(154.78, -7.94) * mm});
            skLineSegment(sketch, "E104.bottom", {"start": v(34.13, 0) * mm, "end": v(57.94, 0) * mm});
            skLineSegment(sketch, "E104.top", {"start": v(34.13, -7.94) * mm, "end": v(57.94, -7.94) * mm});
            skLineSegment(sketch, "E104.left", {"start": v(34.13, 0) * mm, "end": v(34.13, -7.94) * mm});
            skLineSegment(sketch, "E104.right", {"start": v(57.94, 0) * mm, "end": v(57.94, -7.94) * mm});
            skLineSegment(sketch, "E105.bottom", {"start": v(61.91, 35.72) * mm, "end": v(65.88, 35.72) * mm});
            skLineSegment(sketch, "E105.top", {"start": v(61.91, 27.78) * mm, "end": v(65.88, 27.78) * mm});
            skLineSegment(sketch, "E105.left", {"start": v(61.91, 35.72) * mm, "end": v(61.91, 27.78) * mm});
            skLineSegment(sketch, "E105.right", {"start": v(65.88, 35.72) * mm, "end": v(65.88, 27.78) * mm});
            skLineSegment(sketch, "E106.bottom", {"start": v(85.72, 35.72) * mm, "end": v(81.76, 35.72) * mm});
            skLineSegment(sketch, "E106.top", {"start": v(85.72, 27.78) * mm, "end": v(81.76, 27.78) * mm});
            skLineSegment(sketch, "E106.left", {"start": v(85.72, 35.72) * mm, "end": v(85.72, 27.78) * mm});
            skLineSegment(sketch, "E106.right", {"start": v(81.76, 35.72) * mm, "end": v(81.76, 27.78) * mm});
            skSolve(sketch);
        }
        {
            var Q0;
            Q0 = qSketchRegion(id + "F14", true);
            extrude(context, id + "F15", {"entities" : qUnion([Q0]), "operationType" : NewBodyOperationType.ADD, "depth" : 9.52 * mm});
        }
        {
            var Q0;
            Q0=makeQuery(id+"F11.boolean.opBoolean","MERGE",FACE,{"derivedFrom":[makeQuery(id+"F9.boolean.opBoolean","MERGE",FACE,{"derivedFrom":[makeQuery(id+"F1.opExtrude","SWEPT_FACE",FACE,{"disambiguationData":[OSD([sQuery(id+"F0.wireOp",EDGE,"E0.top")])]}),makeQuery(id+"F9.opExtrude","SWEPT_FACE",FACE,{"disambiguationData":[OSD([sQuery(id+"F8.wireOp",EDGE,"E63.top")])]}),makeQuery(id+"F9.opExtrude","SWEPT_FACE",FACE,{"disambiguationData":[OSD([sQuery(id+"F8.wireOp",EDGE,"E64.bottom")])]})]}),makeQuery(id+"F11.opExtrude","SWEPT_FACE",FACE,{"disambiguationData":[OSD([sQuery(id+"F10.wireOp",EDGE,"E72.top")])]})]});
            var sketch = newSketch(context, id + "F16", { "sketchPlane" : qUnion([Q0])});
            skLineSegment(sketch, "E107.bottom", {"start": v(158.75, 65.09) * mm, "end": v(154.78, 65.09) * mm});
            skLineSegment(sketch, "E107.top", {"start": v(158.75, 41.28) * mm, "end": v(154.78, 41.28) * mm});
            skLineSegment(sketch, "E107.left", {"start": v(158.75, 65.09) * mm, "end": v(158.75, 41.28) * mm});
            skLineSegment(sketch, "E107.right", {"start": v(154.78, 65.09) * mm, "end": v(154.78, 41.28) * mm});
            skLineSegment(sketch, "E108.bottom", {"start": v(130.97, 65.09) * mm, "end": v(127, 65.09) * mm});
            skLineSegment(sketch, "E108.top", {"start": v(130.97, 41.28) * mm, "end": v(127, 41.28) * mm});
            skLineSegment(sketch, "E108.left", {"start": v(130.97, 65.09) * mm, "end": v(130.97, 41.28) * mm});
            skLineSegment(sketch, "E108.right", {"start": v(127, 65.09) * mm, "end": v(127, 41.28) * mm});
            skLineSegment(sketch, "E109", {"start": v(154.78, 41.28) * mm, "end": v(130.97, 41.28) * mm, "construction": true});
            skLineSegment(sketch, "E110", {"start": v(142.88, -9.52) * mm, "end": v(142.88, 41.28) * mm, "construction": true});
            skLineSegment(sketch, "E111", {"start": v(12.7, -9.52) * mm, "end": v(12.7, 41.28) * mm, "construction": true});
            skLineSegment(sketch, "E112", {"start": v(24.6, 41.28) * mm, "end": v(0.8, 41.28) * mm, "construction": true});
            skLineSegment(sketch, "E113.bottom", {"start": v(24.6, 41.28) * mm, "end": v(28.57, 41.28) * mm});
            skLineSegment(sketch, "E113.top", {"start": v(24.6, 65.09) * mm, "end": v(28.57, 65.09) * mm});
            skLineSegment(sketch, "E113.left", {"start": v(24.6, 41.28) * mm, "end": v(24.6, 65.09) * mm});
            skLineSegment(sketch, "E113.right", {"start": v(28.57, 41.28) * mm, "end": v(28.57, 65.09) * mm});
            skLineSegment(sketch, "E114.bottom", {"start": v(0.8, 41.28) * mm, "end": v(-3.17, 41.28) * mm});
            skLineSegment(sketch, "E114.top", {"start": v(0.8, 65.09) * mm, "end": v(-3.17, 65.09) * mm});
            skLineSegment(sketch, "E114.left", {"start": v(0.8, 41.28) * mm, "end": v(0.8, 65.09) * mm});
            skLineSegment(sketch, "E114.right", {"start": v(-3.17, 41.28) * mm, "end": v(-3.17, 65.09) * mm});
            skLineSegment(sketch, "E115", {"start": v(57.94, 41.28) * mm, "end": v(34.13, 41.28) * mm, "construction": true});
            skLineSegment(sketch, "E116", {"start": v(46.04, -9.52) * mm, "end": v(46.04, 41.28) * mm, "construction": true});
            skLineSegment(sketch, "E117.right", {"start": v(61.91, 41.28) * mm, "end": v(61.91, 65.09) * mm});
            skLineSegment(sketch, "E117.left", {"start": v(57.94, 41.28) * mm, "end": v(57.94, 65.09) * mm});
            skLineSegment(sketch, "E118.right", {"start": v(30.16, 41.28) * mm, "end": v(30.16, 65.09) * mm});
            skLineSegment(sketch, "E118.left", {"start": v(34.13, 41.28) * mm, "end": v(34.13, 65.09) * mm});
            skLineSegment(sketch, "E117.bottom", {"start": v(57.94, 41.28) * mm, "end": v(61.91, 41.28) * mm});
            skLineSegment(sketch, "E117.top", {"start": v(57.94, 65.09) * mm, "end": v(61.91, 65.09) * mm});
            skLineSegment(sketch, "E118.top", {"start": v(34.13, 65.09) * mm, "end": v(30.16, 65.09) * mm});
            skLineSegment(sketch, "E118.bottom", {"start": v(34.13, 41.28) * mm, "end": v(30.16, 41.28) * mm});
            skLineSegment(sketch, "E119", {"start": v(121.44, 41.28) * mm, "end": v(97.63, 41.28) * mm, "construction": true});
            skLineSegment(sketch, "E120", {"start": v(109.54, -9.53) * mm, "end": v(109.54, 41.28) * mm, "construction": true});
            skLineSegment(sketch, "E121.right", {"start": v(125.41, 41.27) * mm, "end": v(125.41, 65.09) * mm});
            skLineSegment(sketch, "E121.left", {"start": v(121.44, 41.28) * mm, "end": v(121.44, 65.09) * mm});
            skLineSegment(sketch, "E122.right", {"start": v(93.66, 41.27) * mm, "end": v(93.66, 65.09) * mm});
            skLineSegment(sketch, "E122.left", {"start": v(97.63, 41.28) * mm, "end": v(97.63, 65.09) * mm});
            skLineSegment(sketch, "E121.bottom", {"start": v(121.44, 41.27) * mm, "end": v(125.41, 41.27) * mm});
            skLineSegment(sketch, "E121.top", {"start": v(121.44, 65.09) * mm, "end": v(125.41, 65.09) * mm});
            skLineSegment(sketch, "E122.top", {"start": v(97.63, 65.09) * mm, "end": v(93.66, 65.09) * mm});
            skLineSegment(sketch, "E122.bottom", {"start": v(97.63, 41.27) * mm, "end": v(93.66, 41.27) * mm});
            skLineSegment(sketch, "E123", {"start": v(46.04, 179.39) * mm, "end": v(46.04, 128.59) * mm, "construction": true});
            skLineSegment(sketch, "E124", {"start": v(57.94, 128.59) * mm, "end": v(34.13, 128.59) * mm, "construction": true});
            skLineSegment(sketch, "E125.bottom", {"start": v(57.94, 128.59) * mm, "end": v(61.91, 128.59) * mm});
            skLineSegment(sketch, "E125.top", {"start": v(57.94, 104.78) * mm, "end": v(61.91, 104.78) * mm});
            skLineSegment(sketch, "E125.left", {"start": v(57.94, 128.59) * mm, "end": v(57.94, 104.78) * mm});
            skLineSegment(sketch, "E125.right", {"start": v(61.91, 128.59) * mm, "end": v(61.91, 104.78) * mm});
            skLineSegment(sketch, "E126.bottom", {"start": v(34.13, 128.59) * mm, "end": v(30.16, 128.59) * mm});
            skLineSegment(sketch, "E126.top", {"start": v(34.13, 104.78) * mm, "end": v(30.16, 104.78) * mm});
            skLineSegment(sketch, "E126.left", {"start": v(34.13, 128.59) * mm, "end": v(34.13, 104.78) * mm});
            skLineSegment(sketch, "E126.right", {"start": v(30.16, 128.59) * mm, "end": v(30.16, 104.78) * mm});
            skLineSegment(sketch, "E127.right", {"start": v(93.66, 128.59) * mm, "end": v(93.66, 104.78) * mm});
            skLineSegment(sketch, "E127.left", {"start": v(97.63, 128.59) * mm, "end": v(97.63, 104.78) * mm});
            skLineSegment(sketch, "E128", {"start": v(109.54, 179.39) * mm, "end": v(109.54, 128.59) * mm, "construction": true});
            skLineSegment(sketch, "E129.left", {"start": v(121.44, 128.59) * mm, "end": v(121.44, 104.78) * mm});
            skLineSegment(sketch, "E129.right", {"start": v(125.41, 128.59) * mm, "end": v(125.41, 104.78) * mm});
            skLineSegment(sketch, "E130", {"start": v(121.44, 128.59) * mm, "end": v(97.63, 128.59) * mm, "construction": true});
            skLineSegment(sketch, "E127.top", {"start": v(97.63, 104.78) * mm, "end": v(93.66, 104.78) * mm});
            skLineSegment(sketch, "E129.top", {"start": v(121.44, 104.78) * mm, "end": v(125.41, 104.78) * mm});
            skLineSegment(sketch, "E127.bottom", {"start": v(97.63, 128.59) * mm, "end": v(93.66, 128.59) * mm});
            skLineSegment(sketch, "E129.bottom", {"start": v(121.44, 128.59) * mm, "end": v(125.41, 128.59) * mm});
            skLineSegment(sketch, "E131.right", {"start": v(-3.18, 128.59) * mm, "end": v(-3.17, 104.78) * mm});
            skLineSegment(sketch, "E131.left", {"start": v(0.8, 128.59) * mm, "end": v(0.8, 104.78) * mm});
            skLineSegment(sketch, "E132", {"start": v(12.7, 179.39) * mm, "end": v(12.7, 128.59) * mm, "construction": true});
            skLineSegment(sketch, "E133.left", {"start": v(24.6, 128.59) * mm, "end": v(24.6, 104.78) * mm});
            skLineSegment(sketch, "E133.right", {"start": v(28.58, 128.59) * mm, "end": v(28.58, 104.78) * mm});
            skLineSegment(sketch, "E134", {"start": v(24.6, 128.59) * mm, "end": v(0.8, 128.59) * mm, "construction": true});
            skLineSegment(sketch, "E131.top", {"start": v(0.8, 104.78) * mm, "end": v(-3.17, 104.78) * mm});
            skLineSegment(sketch, "E133.top", {"start": v(24.6, 104.78) * mm, "end": v(28.58, 104.78) * mm});
            skLineSegment(sketch, "E131.bottom", {"start": v(0.8, 128.59) * mm, "end": v(-3.17, 128.59) * mm});
            skLineSegment(sketch, "E133.bottom", {"start": v(24.6, 128.59) * mm, "end": v(28.58, 128.59) * mm});
            skLineSegment(sketch, "E135.right", {"start": v(154.78, 128.59) * mm, "end": v(154.78, 104.78) * mm});
            skLineSegment(sketch, "E135.left", {"start": v(158.75, 128.59) * mm, "end": v(158.75, 104.78) * mm});
            skLineSegment(sketch, "E136", {"start": v(142.88, 179.39) * mm, "end": v(142.88, 128.59) * mm, "construction": true});
            skLineSegment(sketch, "E137.left", {"start": v(127, 128.59) * mm, "end": v(127, 104.78) * mm});
            skLineSegment(sketch, "E137.right", {"start": v(130.97, 128.59) * mm, "end": v(130.97, 104.78) * mm});
            skLineSegment(sketch, "E135.top", {"start": v(158.75, 104.78) * mm, "end": v(154.78, 104.78) * mm});
            skLineSegment(sketch, "E137.top", {"start": v(127, 104.78) * mm, "end": v(130.97, 104.78) * mm});
            skLineSegment(sketch, "E135.bottom", {"start": v(158.75, 128.59) * mm, "end": v(154.78, 128.59) * mm});
            skLineSegment(sketch, "E137.bottom", {"start": v(127, 128.59) * mm, "end": v(130.97, 128.59) * mm});
            skLineSegment(sketch, "E138", {"start": v(130.97, 128.59) * mm, "end": v(154.78, 128.59) * mm, "construction": true});
            skSolve(sketch);
        }
        {
            var Q0;
            Q0 = qSketchRegion(id + "F16", true);
            extrude(context, id + "F17", {"entities" : qUnion([Q0]), "operationType" : NewBodyOperationType.ADD, "depth" : 25.4 * mm});
        }
        {
            var Q0;
            Q0=makeQuery(id+"F7.opExtrude","CAP_EDGE",EDGE,{"disambiguationData":[OSD([sQuery(id+"F6.wireOp",EDGE,"E61.bottom")])],"isStart":false});
            var Q1;
            Q1=makeQuery(id+"F7.opExtrude","CAP_EDGE",EDGE,{"disambiguationData":[OSD([sQuery(id+"F6.wireOp",EDGE,"E61.top")])],"isStart":false});
            var Q2;
            Q2=makeQuery(id+"F7.opExtrude","CAP_EDGE",EDGE,{"disambiguationData":[OSD([sQuery(id+"F6.wireOp",EDGE,"E62.bottom")])],"isStart":false});
            var Q3;
            Q3=makeQuery(id+"F7.opExtrude","CAP_EDGE",EDGE,{"disambiguationData":[OSD([sQuery(id+"F6.wireOp",EDGE,"E62.top")])],"isStart":false});
            var Q4;
            Q4=makeQuery(id+"F9.opExtrude","CAP_EDGE",EDGE,{"disambiguationData":[OSD([sQuery(id+"F8.wireOp",EDGE,"E63.bottom")])],"isStart":false});
            var Q5;
            Q5=makeQuery(id+"F9.opExtrude","CAP_EDGE",EDGE,{"disambiguationData":[OSD([sQuery(id+"F8.wireOp",EDGE,"E63.top")])],"isStart":false});
            var Q6;
            Q6=makeQuery(id+"F9.opExtrude","CAP_EDGE",EDGE,{"disambiguationData":[OSD([sQuery(id+"F8.wireOp",EDGE,"E64.top")])],"isStart":false});
            var Q7;
            Q7=makeQuery(id+"F9.opExtrude","CAP_EDGE",EDGE,{"disambiguationData":[OSD([sQuery(id+"F8.wireOp",EDGE,"E64.bottom")])],"isStart":false});
            var Q8;
            Q8=makeQuery(id+"F9.opExtrude","CAP_EDGE",EDGE,{"disambiguationData":[OSD([sQuery(id+"F8.wireOp",EDGE,"E69.bottom")])],"isStart":false});
            var Q9;
            Q9=makeQuery(id+"F9.opExtrude","CAP_EDGE",EDGE,{"disambiguationData":[OSD([sQuery(id+"F8.wireOp",EDGE,"E69.top")])],"isStart":false});
            var Q10;
            Q10=makeQuery(id+"F9.opExtrude","CAP_EDGE",EDGE,{"disambiguationData":[OSD([sQuery(id+"F8.wireOp",EDGE,"E70.bottom")])],"isStart":false});
            var Q11;
            Q11=makeQuery(id+"F9.opExtrude","CAP_EDGE",EDGE,{"disambiguationData":[OSD([sQuery(id+"F8.wireOp",EDGE,"E70.top")])],"isStart":false});
            var Q12;
            Q12=makeQuery(id+"F15.opExtrude","CAP_EDGE",EDGE,{"disambiguationData":[OSD([sQuery(id+"F14.wireOp",EDGE,"E101.bottom")])],"isStart":false});
            var Q13;
            Q13=makeQuery(id+"F15.opExtrude","CAP_EDGE",EDGE,{"disambiguationData":[OSD([sQuery(id+"F14.wireOp",EDGE,"E101.top")])],"isStart":false});
            var Q14;
            Q14=makeQuery(id+"F15.opExtrude","CAP_EDGE",EDGE,{"disambiguationData":[OSD([sQuery(id+"F14.wireOp",EDGE,"4b4f8189-ca04-4867-b59c-8443ad1b2a40.bottom")])],"isStart":false});
            var Q15;
            Q15=makeQuery(id+"F15.opExtrude","CAP_EDGE",EDGE,{"disambiguationData":[OSD([sQuery(id+"F14.wireOp",EDGE,"4b4f8189-ca04-4867-b59c-8443ad1b2a40.top")])],"isStart":false});
            var Q16;
            Q16=makeQuery(id+"F15.opExtrude","CAP_EDGE",EDGE,{"disambiguationData":[OSD([sQuery(id+"F14.wireOp",EDGE,"E102.bottom")])],"isStart":false});
            var Q17;
            Q17=makeQuery(id+"F15.opExtrude","CAP_EDGE",EDGE,{"disambiguationData":[OSD([sQuery(id+"F14.wireOp",EDGE,"E103.bottom")])],"isStart":false});
            var Q18;
            Q18=makeQuery(id+"F15.opExtrude","CAP_EDGE",EDGE,{"disambiguationData":[OSD([sQuery(id+"F14.wireOp",EDGE,"E102.top")])],"isStart":false});
            var Q19;
            Q19=makeQuery(id+"F15.opExtrude","CAP_EDGE",EDGE,{"disambiguationData":[OSD([sQuery(id+"F14.wireOp",EDGE,"E103.top")])],"isStart":false});
            var Q20;
            Q20=makeQuery(id+"F15.opExtrude","CAP_EDGE",EDGE,{"disambiguationData":[OSD([sQuery(id+"F14.wireOp",EDGE,"E104.bottom")])],"isStart":false});
            var Q21;
            Q21=makeQuery(id+"F15.opExtrude","CAP_EDGE",EDGE,{"disambiguationData":[OSD([sQuery(id+"F14.wireOp",EDGE,"E104.top")])],"isStart":false});
            var Q22;
            Q22=makeQuery(id+"F15.opExtrude","CAP_EDGE",EDGE,{"disambiguationData":[OSD([sQuery(id+"F14.wireOp",EDGE,"E105.bottom")])],"isStart":false});
            var Q23;
            Q23=makeQuery(id+"F15.opExtrude","CAP_EDGE",EDGE,{"disambiguationData":[OSD([sQuery(id+"F14.wireOp",EDGE,"E105.top")])],"isStart":false});
            var Q24;
            Q24=makeQuery(id+"F15.opExtrude","CAP_EDGE",EDGE,{"disambiguationData":[OSD([sQuery(id+"F14.wireOp",EDGE,"E106.bottom")])],"isStart":false});
            var Q25;
            Q25=makeQuery(id+"F15.opExtrude","CAP_EDGE",EDGE,{"disambiguationData":[OSD([sQuery(id+"F14.wireOp",EDGE,"E106.top")])],"isStart":false});
            fillet(context, id + "F18", {"entities" : qUnion([Q0, Q1, Q2, Q3, Q4, Q5, Q6, Q7, Q8, Q9, Q10, Q11, Q12, Q13, Q14, Q15, Q16, Q17, Q18, Q19, Q20, Q21, Q22, Q23, Q24, Q25]), "radius" : 3.97 * mm, "tangentPropagation" : true, "allowEdgeOverflow" : false});
        }
        {
            var Q0;
            Q0=makeQuery(id+"F11.boolean.opBoolean","MERGE",FACE,{"derivedFrom":[makeQuery(id+"F9.boolean.opBoolean","MERGE",FACE,{"derivedFrom":[makeQuery(id+"F1.opExtrude","SWEPT_FACE",FACE,{"disambiguationData":[OSD([sQuery(id+"F0.wireOp",EDGE,"E0.top")])]}),makeQuery(id+"F9.opExtrude","SWEPT_FACE",FACE,{"disambiguationData":[OSD([sQuery(id+"F8.wireOp",EDGE,"E63.top")])]}),makeQuery(id+"F9.opExtrude","SWEPT_FACE",FACE,{"disambiguationData":[OSD([sQuery(id+"F8.wireOp",EDGE,"E64.bottom")])]}),makeQuery(id+"F9.opExtrude","SWEPT_FACE",FACE,{"disambiguationData":[OSD([sQuery(id+"F8.wireOp",EDGE,"E69.top")])]}),makeQuery(id+"F9.opExtrude","SWEPT_FACE",FACE,{"disambiguationData":[OSD([sQuery(id+"F8.wireOp",EDGE,"E70.top")])]})]}),makeQuery(id+"F11.opExtrude","SWEPT_FACE",FACE,{"disambiguationData":[OSD([sQuery(id+"F10.wireOp",EDGE,"E72.top")])]})]});
            var sketch = newSketch(context, id + "F19", { "sketchPlane" : qUnion([Q0])});
            skLineSegment(sketch, "E139", {"start": v(154.78, 45.24) * mm, "end": v(130.97, 45.24) * mm, "construction": true});
            skLineSegment(sketch, "E140", {"start": v(24.6, 45.24) * mm, "end": v(0.8, 45.24) * mm, "construction": true});
            skLineSegment(sketch, "E141", {"start": v(142.87, 45.24) * mm, "end": v(142.87, 7.14) * mm, "construction": true});
            skLineSegment(sketch, "E142", {"start": v(12.7, 45.24) * mm, "end": v(12.7, 7.14) * mm, "construction": true});
            skCircle(sketch, "E143", {"center": v(142.88, 7.14) * mm, "radius": 3.18 * mm});
            skCircle(sketch, "E144", {"center": v(142.87, 45.24) * mm, "radius": 3.18 * mm});
            skCircle(sketch, "E145", {"center": v(12.7, 45.24) * mm, "radius": 3.18 * mm});
            skCircle(sketch, "E146", {"center": v(12.7, 7.14) * mm, "radius": 3.18 * mm});
            skLineSegment(sketch, "E147", {"start": v(130.97, 124.62) * mm, "end": v(154.78, 124.62) * mm, "construction": true});
            skLineSegment(sketch, "E148", {"start": v(97.63, 124.62) * mm, "end": v(121.44, 124.62) * mm, "construction": true});
            skLineSegment(sketch, "E149", {"start": v(97.63, 45.24) * mm, "end": v(121.44, 45.24) * mm, "construction": true});
            skLineSegment(sketch, "E150", {"start": v(142.87, 45.24) * mm, "end": v(142.87, 124.62) * mm, "construction": true});
            skLineSegment(sketch, "E151", {"start": v(142.87, 84.93) * mm, "end": v(158.75, 84.93) * mm, "construction": true});
            skLineSegment(sketch, "E152", {"start": v(142.87, 124.62) * mm, "end": v(142.87, 162.72) * mm, "construction": true});
            skLineSegment(sketch, "E153", {"start": v(109.54, 124.62) * mm, "end": v(109.54, 162.72) * mm, "construction": true});
            skLineSegment(sketch, "E154", {"start": v(109.54, 45.24) * mm, "end": v(109.54, 7.14) * mm, "construction": true});
            skCircle(sketch, "E155", {"center": v(142.88, 162.72) * mm, "radius": 3.18 * mm});
            skCircle(sketch, "E156", {"center": v(109.54, 162.72) * mm, "radius": 3.18 * mm});
            skCircle(sketch, "E157", {"center": v(109.54, 124.62) * mm, "radius": 3.18 * mm});
            skCircle(sketch, "E158", {"center": v(142.87, 124.62) * mm, "radius": 3.18 * mm});
            skCircle(sketch, "E159", {"center": v(109.54, 45.24) * mm, "radius": 3.18 * mm});
            skCircle(sketch, "E160", {"center": v(109.54, 7.14) * mm, "radius": 3.18 * mm});
            skSolve(sketch);
        }
        {
            var Q0;
            Q0 = qSketchRegion(id + "F19", true);
            var Q1;
            Q1=makeQuery(id+"F11.boolean.opBoolean","MERGE",FACE,{"derivedFrom":[makeQuery(id+"F9.boolean.opBoolean","MERGE",FACE,{"derivedFrom":[makeQuery(id+"F1.opExtrude","SWEPT_FACE",FACE,{"disambiguationData":[OSD([sQuery(id+"F0.wireOp",EDGE,"E0.bottom")])]}),makeQuery(id+"F9.opExtrude","SWEPT_FACE",FACE,{"disambiguationData":[OSD([sQuery(id+"F8.wireOp",EDGE,"E63.bottom")])]}),makeQuery(id+"F9.opExtrude","SWEPT_FACE",FACE,{"disambiguationData":[OSD([sQuery(id+"F8.wireOp",EDGE,"E64.top")])]}),makeQuery(id+"F9.opExtrude","SWEPT_FACE",FACE,{"disambiguationData":[OSD([sQuery(id+"F8.wireOp",EDGE,"E69.bottom")])]}),makeQuery(id+"F9.opExtrude","SWEPT_FACE",FACE,{"disambiguationData":[OSD([sQuery(id+"F8.wireOp",EDGE,"E70.bottom")])]})]}),makeQuery(id+"F11.opExtrude","SWEPT_FACE",FACE,{"disambiguationData":[OSD([sQuery(id+"F10.wireOp",EDGE,"E74.top")])]})]});
            extrude(context, id + "F20", {"entities" : qUnion([Q0]), "operationType" : NewBodyOperationType.REMOVE, "endBound" : BoundingType.UP_TO_SURFACE, "oppositeDirection" : true, "endBoundEntityFace" : qUnion([Q1]), "depth" : 25.4 * mm});
        }
        {
            var Q0;
            Q0=makeQuery(id+"F1.opExtrude","SWEPT_FACE",FACE,{"disambiguationData":[OSD([sQuery(id+"F0.wireOp",EDGE,"E11")])]});
            var sketch = newSketch(context, id + "F21", { "sketchPlane" : qUnion([Q0])});
            skCircle(sketch, "E161", {"center": v(-3.97, -5.56) * mm, "radius": 2.54 * mm});
            skCircle(sketch, "E162", {"center": v(31.75, 84.93) * mm, "radius": 2.54 * mm});
            skLineSegment(sketch, "E163", {"start": v(31.75, 84.93) * mm, "end": v(31.75, 39.69) * mm, "construction": true});
            skLineSegment(sketch, "E164.rect.bottom", {"start": v(29.34, -6.4) * mm, "end": v(34.16, -6.4) * mm});
            skLineSegment(sketch, "E164.rect.top", {"start": v(29.34, -4.71) * mm, "end": v(34.16, -4.71) * mm});
            skLineSegment(sketch, "E164.rect.left", {"start": v(29.34, -6.4) * mm, "end": v(29.34, -4.71) * mm});
            skLineSegment(sketch, "E164.rect.right", {"start": v(34.16, -6.4) * mm, "end": v(34.16, -4.71) * mm});
            skPoint(sketch, "E164.rect.middle", {"position": v(31.75, -5.56) * mm});
            skLineSegment(sketch, "E165.rect.bottom", {"start": v(30.9, -7.97) * mm, "end": v(32.6, -7.97) * mm});
            skLineSegment(sketch, "E165.rect.top", {"start": v(30.9, -3.14) * mm, "end": v(32.6, -3.14) * mm});
            skLineSegment(sketch, "E165.rect.left", {"start": v(30.9, -7.97) * mm, "end": v(30.9, -3.14) * mm});
            skLineSegment(sketch, "E165.rect.right", {"start": v(32.6, -7.97) * mm, "end": v(32.6, -3.14) * mm});
            skLineSegment(sketch, "E166.bottom", {"start": v(-7.94, 65.09) * mm, "end": v(-33.34, 65.09) * mm});
            skLineSegment(sketch, "E166.top", {"start": v(-7.94, 41.27) * mm, "end": v(-33.34, 41.27) * mm});
            skLineSegment(sketch, "E166.left", {"start": v(-7.94, 65.09) * mm, "end": v(-7.94, 41.27) * mm, "construction": true});
            skLineSegment(sketch, "E166.right", {"start": v(-33.34, 65.09) * mm, "end": v(-33.34, 41.27) * mm});
            skLineSegment(sketch, "E167", {"start": v(-7.94, 65.09) * mm, "end": v(-22.85, 47.84) * mm});
            skArc(sketch, "E168", {"start": v(-22.85, 47.84) * mm, "mid": v(-23.45, 43.6) * mm, "end": v(-19.84, 41.27) * mm});
            skLineSegment(sketch, "E169", {"start": v(-19.84, 45.24) * mm, "end": v(-3.97, 45.24) * mm, "construction": true});
            skLineSegment(sketch, "E170", {"start": v(-3.97, 45.24) * mm, "end": v(-3.97, -5.56) * mm, "construction": true});
            skLineSegment(sketch, "E171.rect.bottom", {"start": v(-17.43, 44.4) * mm, "end": v(-22.26, 44.4) * mm});
            skLineSegment(sketch, "E171.rect.top", {"start": v(-17.43, 46.09) * mm, "end": v(-22.26, 46.09) * mm});
            skLineSegment(sketch, "E171.rect.left", {"start": v(-17.43, 44.4) * mm, "end": v(-17.43, 46.09) * mm});
            skLineSegment(sketch, "E171.rect.right", {"start": v(-22.26, 44.4) * mm, "end": v(-22.26, 46.09) * mm});
            skLineSegment(sketch, "E172.rect.bottom", {"start": v(-20.69, 42.83) * mm, "end": v(-19, 42.83) * mm});
            skLineSegment(sketch, "E172.rect.top", {"start": v(-20.69, 47.66) * mm, "end": v(-19, 47.66) * mm});
            skLineSegment(sketch, "E172.rect.left", {"start": v(-20.69, 42.83) * mm, "end": v(-20.69, 47.66) * mm});
            skLineSegment(sketch, "E172.rect.right", {"start": v(-19, 42.83) * mm, "end": v(-19, 47.66) * mm});
            skCircle(sketch, "E173", {"center": v(-3.97, 175.42) * mm, "radius": 2.54 * mm});
            skLineSegment(sketch, "E174.bottom", {"start": v(-7.94, 128.59) * mm, "end": v(-33.34, 128.59) * mm});
            skLineSegment(sketch, "E174.top", {"start": v(-7.94, 104.78) * mm, "end": v(-33.34, 104.78) * mm});
            skLineSegment(sketch, "E174.left", {"start": v(-7.94, 128.59) * mm, "end": v(-7.94, 104.78) * mm, "construction": true});
            skLineSegment(sketch, "E174.right", {"start": v(-33.34, 128.59) * mm, "end": v(-33.34, 104.78) * mm});
            skArc(sketch, "E175", {"start": v(-19.84, 128.59) * mm, "mid": v(-23.45, 126.27) * mm, "end": v(-22.85, 122.02) * mm});
            skLineSegment(sketch, "E176", {"start": v(-7.94, 104.78) * mm, "end": v(-22.85, 122.02) * mm});
            skLineSegment(sketch, "E177.rect.bottom", {"start": v(-22.26, 123.77) * mm, "end": v(-17.43, 123.77) * mm});
            skLineSegment(sketch, "E177.rect.top", {"start": v(-22.26, 125.46) * mm, "end": v(-17.43, 125.46) * mm});
            skLineSegment(sketch, "E177.rect.left", {"start": v(-22.26, 123.77) * mm, "end": v(-22.26, 125.46) * mm});
            skLineSegment(sketch, "E177.rect.right", {"start": v(-17.43, 123.77) * mm, "end": v(-17.43, 125.46) * mm});
            skLineSegment(sketch, "E178.rect.bottom", {"start": v(-20.69, 122.2) * mm, "end": v(-19, 122.2) * mm});
            skLineSegment(sketch, "E178.rect.top", {"start": v(-20.69, 127.03) * mm, "end": v(-19, 127.03) * mm});
            skLineSegment(sketch, "E178.rect.left", {"start": v(-20.69, 122.2) * mm, "end": v(-20.69, 127.03) * mm});
            skLineSegment(sketch, "E178.rect.right", {"start": v(-19, 122.2) * mm, "end": v(-19, 127.03) * mm});
            skLineSegment(sketch, "E179.rect.bottom", {"start": v(29.34, 174.57) * mm, "end": v(34.16, 174.57) * mm});
            skLineSegment(sketch, "E179.rect.top", {"start": v(29.34, 176.26) * mm, "end": v(34.16, 176.26) * mm});
            skLineSegment(sketch, "E179.rect.left", {"start": v(29.34, 174.57) * mm, "end": v(29.34, 176.26) * mm});
            skLineSegment(sketch, "E179.rect.right", {"start": v(34.16, 174.57) * mm, "end": v(34.16, 176.26) * mm});
            skPoint(sketch, "E179.rect.middle", {"position": v(31.75, 175.42) * mm});
            skLineSegment(sketch, "E180.rect.bottom", {"start": v(30.9, 177.83) * mm, "end": v(32.6, 177.83) * mm});
            skLineSegment(sketch, "E180.rect.top", {"start": v(30.9, 173) * mm, "end": v(32.6, 173) * mm});
            skLineSegment(sketch, "E180.rect.left", {"start": v(30.9, 177.83) * mm, "end": v(30.9, 173) * mm});
            skLineSegment(sketch, "E180.rect.right", {"start": v(32.6, 177.83) * mm, "end": v(32.6, 173) * mm});
            skSolve(sketch);
        }
        {
            var Q0;
            Q0 = qSketchRegion(id + "F21", true);
            var Q1;
            Q1=makeQuery(id+"F1.opExtrude","SWEPT_FACE",FACE,{"disambiguationData":[OSD([sQuery(id+"F0.wireOp",EDGE,"E1.right")])]});
            extrude(context, id + "F22", {"entities" : qUnion([Q0]), "operationType" : NewBodyOperationType.REMOVE, "endBound" : BoundingType.UP_TO_SURFACE, "oppositeDirection" : true, "endBoundEntityFace" : qUnion([Q1]), "depth" : 25.4 * mm});
        }
        {
            var Q0;
            {var subQ0=sQuery(id+"F12.wireOp",EDGE,"E94.top");var subQ1=sQuery(id+"F12.wireOp",EDGE,"E92");var subQ3=sQuery(id+"F12.wireOp",EDGE,"E89.right");var subQ4=sQuery(id+"F12.wireOp",EDGE,"E89.left");var subQ5=sQuery(id+"F12.wireOp",EDGE,"E89.top");var subQ7=sQuery(id+"F12.wireOp",EDGE,"E94.right");var subQ8=sQuery(id+"F12.wireOp",EDGE,"E94.left");var subQ9=sQuery(id+"F12.wireOp",EDGE,"E99");Q0=makeQuery(id+"F13.boolean.opBoolean","SPLIT",FACE,{"disambiguationData":[TD([makeQuery(id+"F1.opExtrude","SWEPT_FACE",FACE,{"disambiguationData":[OSD([sQuery(id+"F0.wireOp",EDGE,"E12")])]})])],"derivedFrom":makeQuery(id+"F13.opExtrude","CAP_FACE",FACE,{"disambiguationData":[OSD([sQuery(id+"F12.wireOp",EDGE,"E83.top"),sQuery(id+"F12.wireOp",EDGE,"E83.left"),sQuery(id+"F12.wireOp",EDGE,"E83.right"),sQuery(id+"F12.wireOp",EDGE,"E84"),sQuery(id+"F12.wireOp",EDGE,"E85.top"),sQuery(id+"F12.wireOp",EDGE,"E85.left"),sQuery(id+"F12.wireOp",EDGE,"E85.right"),sQuery(id+"F12.wireOp",EDGE,"E86"),sQuery(id+"F12.wireOp",EDGE,"E87.bottom"),sQuery(id+"F12.wireOp",EDGE,"E87.top"),sQuery(id+"F12.wireOp",EDGE,"E87.left"),sQuery(id+"F12.wireOp",EDGE,"E87.right"),sQuery(id+"F12.wireOp",EDGE,"E88.bottom"),sQuery(id+"F12.wireOp",EDGE,"E88.left"),sQuery(id+"F12.wireOp",EDGE,"E88.right"),sQuery(id+"F12.wireOp",EDGE,"E89.bottom"),subQ5,subQ4,subQ3,sQuery(id+"F12.wireOp",EDGE,"E90"),sQuery(id+"F12.wireOp",EDGE,"E91"),subQ1,sQuery(id+"F12.wireOp",EDGE,"E93.top"),sQuery(id+"F12.wireOp",EDGE,"E93.left"),sQuery(id+"F12.wireOp",EDGE,"E93.right"),subQ0,subQ8,subQ7,sQuery(id+"F12.wireOp",EDGE,"E97.top"),sQuery(id+"F12.wireOp",EDGE,"E97.left"),sQuery(id+"F12.wireOp",EDGE,"E97.right"),subQ9])],"isStart":true})});}
            var sketch = newSketch(context, id + "F23", { "sketchPlane" : qUnion([Q0])});
            skLineSegment(sketch, "E181", {"start": v(146.84, -38.1) * mm, "end": v(146.84, -31.75) * mm, "construction": true});
            skLineSegment(sketch, "E182", {"start": v(146.84, -31.75) * mm, "end": v(153.2, -31.75) * mm, "construction": true});
            skLineSegment(sketch, "E183", {"start": v(2.38, -31.75) * mm, "end": v(8.73, -31.75) * mm, "construction": true});
            skLineSegment(sketch, "E184", {"start": v(8.73, -31.75) * mm, "end": v(8.73, -38.1) * mm, "construction": true});
            skLineSegment(sketch, "E185", {"start": v(8.73, -31.75) * mm, "end": v(19.84, -31.75) * mm, "construction": true});
            skLineSegment(sketch, "E186", {"start": v(19.84, -31.75) * mm, "end": v(30.96, -31.75) * mm, "construction": true});
            skLineSegment(sketch, "E187", {"start": v(30.96, -31.75) * mm, "end": v(42.07, -31.75) * mm, "construction": true});
            skLineSegment(sketch, "E188", {"start": v(42.07, -31.75) * mm, "end": v(48.42, -31.75) * mm, "construction": true});
            skLineSegment(sketch, "E189", {"start": v(146.84, -31.75) * mm, "end": v(135.73, -31.75) * mm, "construction": true});
            skLineSegment(sketch, "E190", {"start": v(135.73, -31.75) * mm, "end": v(124.62, -31.75) * mm, "construction": true});
            skLineSegment(sketch, "E191", {"start": v(124.62, -31.75) * mm, "end": v(113.5, -31.75) * mm, "construction": true});
            skCircle(sketch, "E192", {"center": v(146.84, -31.75) * mm, "radius": 4.76 * mm});
            skCircle(sketch, "E193", {"center": v(135.73, -31.75) * mm, "radius": 4.76 * mm});
            skCircle(sketch, "E194", {"center": v(124.62, -31.75) * mm, "radius": 4.76 * mm});
            skCircle(sketch, "E195", {"center": v(113.5, -31.75) * mm, "radius": 4.76 * mm});
            skCircle(sketch, "E196", {"center": v(8.73, -31.75) * mm, "radius": 4.76 * mm});
            skCircle(sketch, "E197", {"center": v(19.84, -31.75) * mm, "radius": 4.76 * mm});
            skCircle(sketch, "E198", {"center": v(30.96, -31.75) * mm, "radius": 4.76 * mm});
            skCircle(sketch, "E199", {"center": v(42.07, -31.75) * mm, "radius": 4.76 * mm});
            skSolve(sketch);
        }
        {
            var Q0;
            Q0 = qSketchRegion(id + "F23", true);
            extrude(context, id + "F24", {"entities" : qUnion([Q0]), "operationType" : NewBodyOperationType.REMOVE, "oppositeDirection" : true, "depth" : 38.1 * mm});
        }
        {
            var Q0;
            Q0=makeQuery(id+"F1.opExtrude","SWEPT_FACE",FACE,{"disambiguationData":[OSD([sQuery(id+"F0.wireOp",EDGE,"E10.top")])]});
            var sketch = newSketch(context, id + "F25", { "sketchPlane" : qUnion([Q0])});
            skLineSegment(sketch, "E200", {"start": v(-146.84, 39.69) * mm, "end": v(-146.84, 30.96) * mm, "construction": true});
            skLineSegment(sketch, "E201", {"start": v(-146.84, 30.96) * mm, "end": v(-146.84, 21.43) * mm, "construction": true});
            skLineSegment(sketch, "E202", {"start": v(-146.84, 21.43) * mm, "end": v(-146.84, 11.9) * mm, "construction": true});
            skLineSegment(sketch, "E203", {"start": v(-135.73, 39.69) * mm, "end": v(-135.73, 30.96) * mm, "construction": true});
            skLineSegment(sketch, "E204", {"start": v(-135.73, 30.96) * mm, "end": v(-135.73, 21.43) * mm, "construction": true});
            skLineSegment(sketch, "E205", {"start": v(-135.73, 21.43) * mm, "end": v(-135.73, 11.9) * mm, "construction": true});
            skCircle(sketch, "E206", {"center": v(-135.73, 11.9) * mm, "radius": 0.8 * mm});
            skCircle(sketch, "E207", {"center": v(-146.84, 11.9) * mm, "radius": 0.8 * mm});
            skCircle(sketch, "E208", {"center": v(-146.84, 21.43) * mm, "radius": 0.8 * mm});
            skCircle(sketch, "E209", {"center": v(-135.73, 21.43) * mm, "radius": 0.8 * mm});
            skCircle(sketch, "E210", {"center": v(-135.73, 30.96) * mm, "radius": 0.8 * mm});
            skCircle(sketch, "E211", {"center": v(-146.84, 30.96) * mm, "radius": 0.8 * mm});
            skLineSegment(sketch, "E212", {"start": v(-124.62, 21.43) * mm, "end": v(-124.62, 11.9) * mm, "construction": true});
            skLineSegment(sketch, "E213", {"start": v(-124.62, 30.96) * mm, "end": v(-124.62, 21.43) * mm, "construction": true});
            skLineSegment(sketch, "E214", {"start": v(-124.62, 39.69) * mm, "end": v(-124.62, 30.96) * mm, "construction": true});
            skCircle(sketch, "E215", {"center": v(-124.62, 11.9) * mm, "radius": 0.8 * mm});
            skCircle(sketch, "E216", {"center": v(-124.62, 21.43) * mm, "radius": 0.8 * mm});
            skCircle(sketch, "E217", {"center": v(-124.62, 30.96) * mm, "radius": 0.8 * mm});
            skLineSegment(sketch, "E218", {"start": v(-113.5, 21.43) * mm, "end": v(-113.5, 11.9) * mm, "construction": true});
            skLineSegment(sketch, "E219", {"start": v(-113.5, 30.96) * mm, "end": v(-113.5, 21.43) * mm, "construction": true});
            skLineSegment(sketch, "E220", {"start": v(-113.5, 39.69) * mm, "end": v(-113.5, 30.96) * mm, "construction": true});
            skCircle(sketch, "E221", {"center": v(-113.5, 11.9) * mm, "radius": 0.8 * mm});
            skCircle(sketch, "E222", {"center": v(-113.5, 21.43) * mm, "radius": 0.8 * mm});
            skCircle(sketch, "E223", {"center": v(-113.5, 30.96) * mm, "radius": 0.8 * mm});
            skLineSegment(sketch, "E224", {"start": v(-30.96, 39.69) * mm, "end": v(-30.96, 30.96) * mm, "construction": true});
            skLineSegment(sketch, "E225", {"start": v(-42.07, 21.43) * mm, "end": v(-42.07, 11.9) * mm, "construction": true});
            skLineSegment(sketch, "E226", {"start": v(-30.96, 21.43) * mm, "end": v(-30.96, 11.9) * mm, "construction": true});
            skLineSegment(sketch, "E227", {"start": v(-42.07, 39.69) * mm, "end": v(-42.07, 30.96) * mm, "construction": true});
            skLineSegment(sketch, "E228", {"start": v(-30.96, 30.96) * mm, "end": v(-30.96, 21.43) * mm, "construction": true});
            skLineSegment(sketch, "E229", {"start": v(-42.07, 30.96) * mm, "end": v(-42.07, 21.43) * mm, "construction": true});
            skCircle(sketch, "E230", {"center": v(-42.07, 11.9) * mm, "radius": 0.8 * mm});
            skCircle(sketch, "E231", {"center": v(-30.96, 11.9) * mm, "radius": 0.8 * mm});
            skCircle(sketch, "E232", {"center": v(-42.07, 21.43) * mm, "radius": 0.8 * mm});
            skCircle(sketch, "E233", {"center": v(-30.96, 21.43) * mm, "radius": 0.8 * mm});
            skCircle(sketch, "E234", {"center": v(-42.07, 30.96) * mm, "radius": 0.8 * mm});
            skCircle(sketch, "E235", {"center": v(-30.96, 30.96) * mm, "radius": 0.8 * mm});
            skLineSegment(sketch, "E236", {"start": v(-8.73, 39.69) * mm, "end": v(-8.73, 30.96) * mm, "construction": true});
            skLineSegment(sketch, "E237", {"start": v(-19.84, 21.43) * mm, "end": v(-19.84, 11.9) * mm, "construction": true});
            skLineSegment(sketch, "E238", {"start": v(-8.73, 21.43) * mm, "end": v(-8.73, 11.9) * mm, "construction": true});
            skLineSegment(sketch, "E239", {"start": v(-19.84, 39.69) * mm, "end": v(-19.84, 30.96) * mm, "construction": true});
            skLineSegment(sketch, "E240", {"start": v(-8.73, 30.96) * mm, "end": v(-8.73, 21.43) * mm, "construction": true});
            skLineSegment(sketch, "E241", {"start": v(-19.84, 30.96) * mm, "end": v(-19.84, 21.43) * mm, "construction": true});
            skCircle(sketch, "E242", {"center": v(-19.84, 11.9) * mm, "radius": 0.8 * mm});
            skCircle(sketch, "E243", {"center": v(-8.73, 11.9) * mm, "radius": 0.8 * mm});
            skCircle(sketch, "E244", {"center": v(-19.84, 21.43) * mm, "radius": 0.8 * mm});
            skCircle(sketch, "E245", {"center": v(-8.73, 21.43) * mm, "radius": 0.8 * mm});
            skCircle(sketch, "E246", {"center": v(-19.84, 30.96) * mm, "radius": 0.8 * mm});
            skCircle(sketch, "E247", {"center": v(-8.73, 30.96) * mm, "radius": 0.8 * mm});
            skLineSegment(sketch, "E248", {"start": v(-146.84, 130.18) * mm, "end": v(-146.84, 138.9) * mm, "construction": true});
            skLineSegment(sketch, "E249", {"start": v(-146.84, 138.9) * mm, "end": v(-146.84, 148.43) * mm, "construction": true});
            skLineSegment(sketch, "E250", {"start": v(-146.84, 148.43) * mm, "end": v(-146.84, 157.96) * mm, "construction": true});
            skCircle(sketch, "E251", {"center": v(-146.84, 157.96) * mm, "radius": 0.8 * mm});
            skCircle(sketch, "E252", {"center": v(-146.84, 148.43) * mm, "radius": 0.8 * mm});
            skCircle(sketch, "E253", {"center": v(-146.84, 138.9) * mm, "radius": 0.8 * mm});
            skLineSegment(sketch, "E254", {"start": v(-135.73, 130.18) * mm, "end": v(-135.73, 138.9) * mm, "construction": true});
            skLineSegment(sketch, "E255", {"start": v(-135.73, 138.9) * mm, "end": v(-135.73, 148.43) * mm, "construction": true});
            skLineSegment(sketch, "E256", {"start": v(-135.73, 148.43) * mm, "end": v(-135.73, 157.96) * mm, "construction": true});
            skCircle(sketch, "E257", {"center": v(-135.73, 157.96) * mm, "radius": 0.8 * mm});
            skCircle(sketch, "E258", {"center": v(-135.73, 138.9) * mm, "radius": 0.8 * mm});
            skCircle(sketch, "E259", {"center": v(-135.73, 148.43) * mm, "radius": 0.8 * mm});
            skLineSegment(sketch, "E260", {"start": v(-124.62, 130.18) * mm, "end": v(-124.62, 138.9) * mm, "construction": true});
            skLineSegment(sketch, "E261", {"start": v(-124.62, 138.9) * mm, "end": v(-124.62, 148.43) * mm, "construction": true});
            skLineSegment(sketch, "E262", {"start": v(-124.62, 148.43) * mm, "end": v(-124.62, 157.96) * mm, "construction": true});
            skCircle(sketch, "E263", {"center": v(-124.62, 157.96) * mm, "radius": 0.8 * mm});
            skCircle(sketch, "E264", {"center": v(-124.62, 138.9) * mm, "radius": 0.8 * mm});
            skCircle(sketch, "E265", {"center": v(-124.62, 148.43) * mm, "radius": 0.8 * mm});
            skLineSegment(sketch, "E266", {"start": v(-113.5, 130.18) * mm, "end": v(-113.5, 138.9) * mm, "construction": true});
            skLineSegment(sketch, "E267", {"start": v(-113.5, 138.9) * mm, "end": v(-113.5, 148.43) * mm, "construction": true});
            skLineSegment(sketch, "E268", {"start": v(-113.5, 148.43) * mm, "end": v(-113.5, 157.96) * mm, "construction": true});
            skCircle(sketch, "E269", {"center": v(-113.5, 157.96) * mm, "radius": 0.8 * mm});
            skCircle(sketch, "E270", {"center": v(-113.5, 138.9) * mm, "radius": 0.8 * mm});
            skCircle(sketch, "E271", {"center": v(-113.5, 148.43) * mm, "radius": 0.8 * mm});
            skSolve(sketch);
        }
        {
            var Q0;
            Q0 = qSketchRegion(id + "F25", true);
            var Q1;
            Q1=makeQuery(id+"F3.boolean.opBoolean","COPY",FACE,{"derivedFrom":makeQuery(id+"F3.opExtrude","SWEPT_FACE",FACE,{"disambiguationData":[OSD([sQuery(id+"F2.wireOp",EDGE,"ed1b012a-4aa0-4550-af44-26773e9c228e")])]})});
            extrude(context, id + "F26", {"entities" : qUnion([Q0]), "operationType" : NewBodyOperationType.REMOVE, "oppositeDirection" : true, "endBoundEntityFace" : qUnion([Q1]), "depth" : 3.17 * mm});
        }
        {
            var Q0;
            Q0=makeQuery(id+"F1.opExtrude","SWEPT_FACE",FACE,{"disambiguationData":[OSD([sQuery(id+"F0.wireOp",EDGE,"E23")])]});
            var sketch = newSketch(context, id + "F27", { "sketchPlane" : qUnion([Q0])});
            skLineSegment(sketch, "E272", {"start": v(146.84, 21.43) * mm, "end": v(146.84, 11.9) * mm, "construction": true});
            skLineSegment(sketch, "E273", {"start": v(146.84, 30.96) * mm, "end": v(146.84, 21.43) * mm, "construction": true});
            skCircle(sketch, "E274", {"center": v(146.84, 16.67) * mm, "radius": 0.8 * mm});
            skCircle(sketch, "E275", {"center": v(146.84, 26.2) * mm, "radius": 0.8 * mm});
            skLineSegment(sketch, "E276", {"start": v(135.73, 30.96) * mm, "end": v(135.73, 21.43) * mm, "construction": true});
            skLineSegment(sketch, "E277", {"start": v(135.73, 21.43) * mm, "end": v(135.73, 11.9) * mm, "construction": true});
            skCircle(sketch, "E278", {"center": v(135.73, 16.67) * mm, "radius": 0.8 * mm});
            skCircle(sketch, "E279", {"center": v(135.73, 26.2) * mm, "radius": 0.8 * mm});
            skLineSegment(sketch, "E280", {"start": v(124.62, 30.96) * mm, "end": v(124.62, 21.43) * mm, "construction": true});
            skLineSegment(sketch, "E281", {"start": v(124.62, 21.43) * mm, "end": v(124.62, 11.9) * mm, "construction": true});
            skCircle(sketch, "E282", {"center": v(124.62, 16.67) * mm, "radius": 0.8 * mm});
            skCircle(sketch, "E283", {"center": v(124.62, 26.2) * mm, "radius": 0.8 * mm});
            skLineSegment(sketch, "E284", {"start": v(113.5, 30.96) * mm, "end": v(113.5, 21.43) * mm, "construction": true});
            skLineSegment(sketch, "E285", {"start": v(113.5, 21.43) * mm, "end": v(113.5, 11.9) * mm, "construction": true});
            skCircle(sketch, "E286", {"center": v(113.5, 16.67) * mm, "radius": 0.8 * mm});
            skCircle(sketch, "E287", {"center": v(113.5, 26.2) * mm, "radius": 0.8 * mm});
            skLineSegment(sketch, "E288", {"start": v(42.07, 11.9) * mm, "end": v(42.07, 21.43) * mm, "construction": true});
            skLineSegment(sketch, "E289", {"start": v(42.07, 21.43) * mm, "end": v(42.07, 30.96) * mm, "construction": true});
            skLineSegment(sketch, "E290", {"start": v(30.96, 30.96) * mm, "end": v(30.96, 21.43) * mm, "construction": true});
            skLineSegment(sketch, "E291", {"start": v(30.96, 21.43) * mm, "end": v(30.96, 11.9) * mm, "construction": true});
            skLineSegment(sketch, "E292", {"start": v(19.84, 30.96) * mm, "end": v(19.84, 21.43) * mm, "construction": true});
            skLineSegment(sketch, "E293", {"start": v(19.84, 21.43) * mm, "end": v(19.84, 11.9) * mm, "construction": true});
            skCircle(sketch, "E294", {"center": v(42.07, 26.2) * mm, "radius": 0.8 * mm});
            skCircle(sketch, "E295", {"center": v(30.96, 26.2) * mm, "radius": 0.8 * mm});
            skCircle(sketch, "E296", {"center": v(19.84, 26.2) * mm, "radius": 0.8 * mm});
            skCircle(sketch, "E297", {"center": v(19.84, 16.67) * mm, "radius": 0.8 * mm});
            skCircle(sketch, "E298", {"center": v(30.96, 16.67) * mm, "radius": 0.8 * mm});
            skCircle(sketch, "E299", {"center": v(42.07, 16.67) * mm, "radius": 0.8 * mm});
            skLineSegment(sketch, "E300", {"start": v(8.73, 30.96) * mm, "end": v(8.73, 21.43) * mm, "construction": true});
            skLineSegment(sketch, "E301", {"start": v(8.73, 21.43) * mm, "end": v(8.73, 11.9) * mm, "construction": true});
            skCircle(sketch, "E302", {"center": v(8.73, 26.2) * mm, "radius": 0.8 * mm});
            skCircle(sketch, "E303", {"center": v(8.73, 16.67) * mm, "radius": 0.8 * mm});
            skLineSegment(sketch, "E304", {"start": v(146.84, 138.9) * mm, "end": v(146.84, 148.43) * mm, "construction": true});
            skLineSegment(sketch, "E305", {"start": v(146.84, 148.43) * mm, "end": v(146.84, 157.96) * mm, "construction": true});
            skCircle(sketch, "E306", {"center": v(146.84, 143.67) * mm, "radius": 0.8 * mm});
            skCircle(sketch, "E307", {"center": v(146.84, 153.2) * mm, "radius": 0.8 * mm});
            skLineSegment(sketch, "E308", {"start": v(135.73, 138.9) * mm, "end": v(135.73, 148.43) * mm, "construction": true});
            skLineSegment(sketch, "E309", {"start": v(135.73, 148.43) * mm, "end": v(135.73, 157.96) * mm, "construction": true});
            skLineSegment(sketch, "E310", {"start": v(124.62, 138.9) * mm, "end": v(124.62, 148.43) * mm, "construction": true});
            skLineSegment(sketch, "E311", {"start": v(124.62, 148.43) * mm, "end": v(124.62, 157.96) * mm, "construction": true});
            skLineSegment(sketch, "E312", {"start": v(113.5, 138.9) * mm, "end": v(113.5, 148.43) * mm, "construction": true});
            skLineSegment(sketch, "E313", {"start": v(113.5, 148.43) * mm, "end": v(113.5, 157.96) * mm, "construction": true});
            skCircle(sketch, "E314", {"center": v(135.73, 143.67) * mm, "radius": 0.8 * mm});
            skCircle(sketch, "E315", {"center": v(135.73, 153.2) * mm, "radius": 0.8 * mm});
            skCircle(sketch, "E316", {"center": v(124.62, 153.2) * mm, "radius": 0.8 * mm});
            skCircle(sketch, "E317", {"center": v(124.62, 143.67) * mm, "radius": 0.8 * mm});
            skCircle(sketch, "E318", {"center": v(113.5, 143.67) * mm, "radius": 0.8 * mm});
            skCircle(sketch, "E319", {"center": v(113.5, 153.2) * mm, "radius": 0.8 * mm});
            skSolve(sketch);
        }
        {
            var Q0;
            Q0 = qSketchRegion(id + "F27", true);
            extrude(context, id + "F28", {"entities" : qUnion([Q0]), "operationType" : NewBodyOperationType.REMOVE, "oppositeDirection" : true, "depth" : 6.35 * mm});
        }
        {
            var Q0;
            {var subQ0=sQuery(id+"F12.wireOp",EDGE,"E88.left");var subQ1=sQuery(id+"F12.wireOp",EDGE,"E94.left");var subQ2=sQuery(id+"F12.wireOp",EDGE,"E88.bottom");var subQ3=sQuery(id+"F12.wireOp",EDGE,"E87.right");var subQ4=sQuery(id+"F12.wireOp",EDGE,"E87.left");var subQ5=sQuery(id+"F12.wireOp",EDGE,"E87.bottom");var subQ6=sQuery(id+"F12.wireOp",EDGE,"E86");var subQ7=sQuery(id+"F12.wireOp",EDGE,"E97.top");var subQ8=sQuery(id+"F12.wireOp",EDGE,"E85.right");var subQ9=sQuery(id+"F12.wireOp",EDGE,"E94.right");var subQ10=sQuery(id+"F12.wireOp",EDGE,"E85.top");var subQ11=sQuery(id+"F12.wireOp",EDGE,"E84");var subQ12=sQuery(id+"F12.wireOp",EDGE,"E93.right");var subQ13=sQuery(id+"F12.wireOp",EDGE,"E83.right");var subQ14=sQuery(id+"F12.wireOp",EDGE,"E93.left");var subQ15=sQuery(id+"F12.wireOp",EDGE,"E83.left");var subQ16=sQuery(id+"F12.wireOp",EDGE,"E88.right");var subQ17=sQuery(id+"F12.wireOp",EDGE,"E83.top");var subQ18=sQuery(id+"F12.wireOp",EDGE,"E90");var subQ19=sQuery(id+"F12.wireOp",EDGE,"E94.top");var subQ20=sQuery(id+"F12.wireOp",EDGE,"E91");var subQ21=sQuery(id+"F12.wireOp",EDGE,"E87.top");var subQ22=sQuery(id+"F12.wireOp",EDGE,"E93.top");var subQ23=sQuery(id+"F12.wireOp",EDGE,"E97.right");var subQ24=sQuery(id+"F12.wireOp",EDGE,"E85.left");var subQ25=sQuery(id+"F12.wireOp",EDGE,"E89.right");var subQ26=sQuery(id+"F12.wireOp",EDGE,"E89.bottom");var subQ27=sQuery(id+"F12.wireOp",EDGE,"E89.top");var subQ28=sQuery(id+"F12.wireOp",EDGE,"E89.left");var subQ29=sQuery(id+"F12.wireOp",EDGE,"E92");var subQ30=sQuery(id+"F12.wireOp",EDGE,"E97.left");var subQ31=sQuery(id+"F12.wireOp",EDGE,"E99");Q0=makeQuery(id+"F15.boolean.opBoolean","SPLIT",FACE,{"disambiguationData":[TD([makeQuery(id+"F1.opExtrude","SWEPT_FACE",FACE,{"disambiguationData":[OSD([sQuery(id+"F0.wireOp",EDGE,"E1.left")])]})])],"derivedFrom":makeQuery(id+"F13.opExtrude","CAP_FACE",FACE,{"disambiguationData":[OSD([subQ17,subQ15,subQ13,subQ11,subQ10,subQ24,subQ8,subQ6,subQ5,subQ21,subQ4,subQ3,subQ2,subQ0,subQ16,subQ26,subQ27,subQ28,subQ25,subQ18,subQ20,subQ29,subQ22,subQ14,subQ12,subQ19,subQ1,subQ9,subQ7,subQ30,subQ23,subQ31])],"isStart":false})});}
            var sketch = newSketch(context, id + "F29", { "sketchPlane" : qUnion([Q0])});
            skLineSegment(sketch, "E320.bottom", {"start": v(66.67, 35.72) * mm, "end": v(80.96, 35.72) * mm});
            skLineSegment(sketch, "E320.top", {"start": v(66.67, 31.75) * mm, "end": v(80.96, 31.75) * mm, "construction": true});
            skLineSegment(sketch, "E320.left", {"start": v(66.68, 35.72) * mm, "end": v(66.68, 31.75) * mm});
            skLineSegment(sketch, "E320.right", {"start": v(80.96, 35.72) * mm, "end": v(80.96, 31.75) * mm});
            skPoint(sketch, "E321", {"position": v(73.82, 35.72) * mm});
            skArc(sketch, "E322", {"start": v(66.67, 31.75) * mm, "mid": v(73.82, 24.6) * mm, "end": v(80.96, 31.75) * mm});
            skLineSegment(sketch, "E323", {"start": v(61.91, 25.4) * mm, "end": v(65.69, 25.4) * mm});
            skLineSegment(sketch, "E324", {"start": v(85.72, 25.4) * mm, "end": v(81.95, 25.4) * mm});
            skLineSegment(sketch, "E325", {"start": v(73.82, 31.75) * mm, "end": v(73.82, 24.6) * mm, "construction": true});
            skLineSegment(sketch, "E326", {"start": v(73.82, 24.6) * mm, "end": v(73.82, 21.43) * mm, "construction": true});
            skArc(sketch, "E327", {"start": v(65.69, 25.4) * mm, "mid": v(73.82, 21.43) * mm, "end": v(81.95, 25.4) * mm});
            skLineSegment(sketch, "E328.bottom", {"start": v(61.91, 11.68) * mm, "end": v(85.72, 11.68) * mm});
            skLineSegment(sketch, "E328.left", {"start": v(61.91, 11.68) * mm, "end": v(61.91, 25.4) * mm});
            skLineSegment(sketch, "E328.right", {"start": v(85.72, 11.68) * mm, "end": v(85.72, 25.4) * mm});
            skSolve(sketch);
        }
        {
            var Q0;
            Q0 = qSketchRegion(id + "F29", true);
            var Q1;
            {var subQ0=sQuery(id+"F12.wireOp",EDGE,"E90");var subQ1=sQuery(id+"F12.wireOp",EDGE,"E88.left");var subQ2=sQuery(id+"F12.wireOp",EDGE,"E97.left");var subQ3=sQuery(id+"F12.wireOp",EDGE,"E91");var subQ4=sQuery(id+"F12.wireOp",EDGE,"E88.right");var subQ5=sQuery(id+"F12.wireOp",EDGE,"E86");var subQ6=sQuery(id+"F12.wireOp",EDGE,"E93.top");var subQ9=sQuery(id+"F12.wireOp",EDGE,"E93.right");var subQ10=sQuery(id+"F12.wireOp",EDGE,"E97.right");var subQ11=sQuery(id+"F12.wireOp",EDGE,"E93.left");var subQ12=sQuery(id+"F12.wireOp",EDGE,"E97.top");var subQ13=sQuery(id+"F12.wireOp",EDGE,"E99");Q1=makeQuery(id+"F13.boolean.opBoolean","SPLIT",FACE,{"disambiguationData":[TD([makeQuery(id+"F1.opExtrude","SWEPT_FACE",FACE,{"disambiguationData":[OSD([sQuery(id+"F0.wireOp",EDGE,"E20.right")])]})])],"derivedFrom":makeQuery(id+"F13.opExtrude","CAP_FACE",FACE,{"disambiguationData":[OSD([sQuery(id+"F12.wireOp",EDGE,"E83.top"),sQuery(id+"F12.wireOp",EDGE,"E83.left"),sQuery(id+"F12.wireOp",EDGE,"E83.right"),sQuery(id+"F12.wireOp",EDGE,"E84"),sQuery(id+"F12.wireOp",EDGE,"E85.top"),sQuery(id+"F12.wireOp",EDGE,"E85.left"),sQuery(id+"F12.wireOp",EDGE,"E85.right"),subQ5,sQuery(id+"F12.wireOp",EDGE,"E87.bottom"),sQuery(id+"F12.wireOp",EDGE,"E87.top"),sQuery(id+"F12.wireOp",EDGE,"E87.left"),sQuery(id+"F12.wireOp",EDGE,"E87.right"),sQuery(id+"F12.wireOp",EDGE,"E88.bottom"),subQ1,subQ4,sQuery(id+"F12.wireOp",EDGE,"E89.bottom"),sQuery(id+"F12.wireOp",EDGE,"E89.top"),sQuery(id+"F12.wireOp",EDGE,"E89.left"),sQuery(id+"F12.wireOp",EDGE,"E89.right"),subQ0,subQ3,sQuery(id+"F12.wireOp",EDGE,"E92"),subQ6,subQ11,subQ9,sQuery(id+"F12.wireOp",EDGE,"E94.top"),sQuery(id+"F12.wireOp",EDGE,"E94.left"),sQuery(id+"F12.wireOp",EDGE,"E94.right"),subQ12,subQ2,subQ10,subQ13])],"isStart":true})});}
            extrude(context, id + "F30", {"entities" : qUnion([Q0]), "operationType" : NewBodyOperationType.REMOVE, "endBound" : BoundingType.UP_TO_SURFACE, "oppositeDirection" : true, "endBoundEntityFace" : qUnion([Q1]), "depth" : 25.4 * mm});
        }
        {
            var Q0;
            Q0=makeQuery(id+"F1.opExtrude","SWEPT_FACE",FACE,{"disambiguationData":[OSD([sQuery(id+"F0.wireOp",EDGE,"E23")])]});
            var sketch = newSketch(context, id + "F31", { "sketchPlane" : qUnion([Q0])});
            skCircle(sketch, "E329", {"center": v(146.84, 16.67) * mm, "radius": 0.8 * mm});
            skCircle(sketch, "E330", {"center": v(146.84, 16.67) * mm, "radius": 1.59 * mm});
            skCircle(sketch, "E331", {"center": v(146.84, 26.2) * mm, "radius": 0.8 * mm});
            skCircle(sketch, "E332", {"center": v(146.84, 26.2) * mm, "radius": 1.59 * mm});
            skCircle(sketch, "E333", {"center": v(135.73, 26.2) * mm, "radius": 0.8 * mm});
            skCircle(sketch, "E334", {"center": v(135.73, 26.2) * mm, "radius": 1.59 * mm});
            skCircle(sketch, "E335", {"center": v(135.73, 16.67) * mm, "radius": 0.8 * mm});
            skCircle(sketch, "E336", {"center": v(135.73, 16.67) * mm, "radius": 1.59 * mm});
            skCircle(sketch, "E337", {"center": v(124.62, 16.67) * mm, "radius": 0.8 * mm});
            skCircle(sketch, "E338", {"center": v(124.62, 16.67) * mm, "radius": 1.59 * mm});
            skCircle(sketch, "E339", {"center": v(124.62, 26.2) * mm, "radius": 1.59 * mm});
            skCircle(sketch, "E340", {"center": v(124.62, 26.2) * mm, "radius": 0.8 * mm});
            skCircle(sketch, "E341", {"center": v(113.5, 16.67) * mm, "radius": 0.8 * mm});
            skCircle(sketch, "E342", {"center": v(113.5, 16.67) * mm, "radius": 1.59 * mm});
            skCircle(sketch, "E343", {"center": v(113.5, 26.2) * mm, "radius": 1.59 * mm});
            skCircle(sketch, "E344", {"center": v(113.5, 26.2) * mm, "radius": 0.8 * mm});
            skCircle(sketch, "E345", {"center": v(113.5, 153.2) * mm, "radius": 0.8 * mm});
            skCircle(sketch, "E346", {"center": v(113.5, 153.2) * mm, "radius": 1.59 * mm});
            skCircle(sketch, "E347", {"center": v(113.5, 143.67) * mm, "radius": 0.8 * mm});
            skCircle(sketch, "E348", {"center": v(113.5, 143.67) * mm, "radius": 1.59 * mm});
            skCircle(sketch, "E349", {"center": v(124.62, 153.2) * mm, "radius": 0.8 * mm});
            skCircle(sketch, "E350", {"center": v(124.62, 153.2) * mm, "radius": 1.59 * mm});
            skCircle(sketch, "E351", {"center": v(124.62, 143.67) * mm, "radius": 0.8 * mm});
            skCircle(sketch, "E352", {"center": v(124.62, 143.67) * mm, "radius": 1.59 * mm});
            skCircle(sketch, "E353", {"center": v(135.73, 143.67) * mm, "radius": 0.8 * mm});
            skCircle(sketch, "E354", {"center": v(135.73, 143.67) * mm, "radius": 1.59 * mm});
            skCircle(sketch, "E355", {"center": v(135.73, 153.2) * mm, "radius": 0.8 * mm});
            skCircle(sketch, "E356", {"center": v(135.73, 153.2) * mm, "radius": 1.59 * mm});
            skCircle(sketch, "E357", {"center": v(146.84, 153.2) * mm, "radius": 0.8 * mm});
            skCircle(sketch, "E358", {"center": v(146.84, 153.2) * mm, "radius": 1.59 * mm});
            skCircle(sketch, "E359", {"center": v(146.84, 143.67) * mm, "radius": 0.8 * mm});
            skCircle(sketch, "E360", {"center": v(146.84, 143.67) * mm, "radius": 1.59 * mm});
            skSolve(sketch);
        }
        {
            var Q0;
            Q0 = qSketchRegion(id + "F31", true);
            extrude(context, id + "F32", {"entities" : qUnion([Q0]), "operationType" : NewBodyOperationType.ADD, "depth" : 4.76 * mm});
        }
        {
            var Q0;
            {var subQ0=sQuery(id+"F12.wireOp",EDGE,"E90");var subQ1=sQuery(id+"F12.wireOp",EDGE,"E88.left");var subQ2=sQuery(id+"F12.wireOp",EDGE,"E97.left");var subQ3=sQuery(id+"F12.wireOp",EDGE,"E91");var subQ4=sQuery(id+"F12.wireOp",EDGE,"E88.right");var subQ5=sQuery(id+"F12.wireOp",EDGE,"E86");var subQ6=sQuery(id+"F12.wireOp",EDGE,"E93.top");var subQ9=sQuery(id+"F12.wireOp",EDGE,"E93.right");var subQ10=sQuery(id+"F12.wireOp",EDGE,"E97.right");var subQ11=sQuery(id+"F12.wireOp",EDGE,"E93.left");var subQ12=sQuery(id+"F12.wireOp",EDGE,"E97.top");var subQ13=sQuery(id+"F12.wireOp",EDGE,"E99");Q0=makeQuery(id+"F13.boolean.opBoolean","SPLIT",FACE,{"disambiguationData":[TD([makeQuery(id+"F1.opExtrude","SWEPT_FACE",FACE,{"disambiguationData":[OSD([sQuery(id+"F0.wireOp",EDGE,"E20.right")])]})])],"derivedFrom":makeQuery(id+"F13.opExtrude","CAP_FACE",FACE,{"disambiguationData":[OSD([sQuery(id+"F12.wireOp",EDGE,"E83.top"),sQuery(id+"F12.wireOp",EDGE,"E83.left"),sQuery(id+"F12.wireOp",EDGE,"E83.right"),sQuery(id+"F12.wireOp",EDGE,"E84"),sQuery(id+"F12.wireOp",EDGE,"E85.top"),sQuery(id+"F12.wireOp",EDGE,"E85.left"),sQuery(id+"F12.wireOp",EDGE,"E85.right"),subQ5,sQuery(id+"F12.wireOp",EDGE,"E87.bottom"),sQuery(id+"F12.wireOp",EDGE,"E87.top"),sQuery(id+"F12.wireOp",EDGE,"E87.left"),sQuery(id+"F12.wireOp",EDGE,"E87.right"),sQuery(id+"F12.wireOp",EDGE,"E88.bottom"),subQ1,subQ4,sQuery(id+"F12.wireOp",EDGE,"E89.bottom"),sQuery(id+"F12.wireOp",EDGE,"E89.top"),sQuery(id+"F12.wireOp",EDGE,"E89.left"),sQuery(id+"F12.wireOp",EDGE,"E89.right"),subQ0,subQ3,sQuery(id+"F12.wireOp",EDGE,"E92"),subQ6,subQ11,subQ9,sQuery(id+"F12.wireOp",EDGE,"E94.top"),sQuery(id+"F12.wireOp",EDGE,"E94.left"),sQuery(id+"F12.wireOp",EDGE,"E94.right"),subQ12,subQ2,subQ10,subQ13])],"isStart":true})});}
            extrude(context, id + "F33", {"entities" : qUnion([Q0]), "operationType" : NewBodyOperationType.REMOVE, "oppositeDirection" : true, "depth" : 3.17 * mm});
        }
        {
            var Q0;
            {var subQ0=sQuery(id+"F0.wireOp",EDGE,"E29");var subQ1=sQuery(id+"F0.wireOp",EDGE,"E22.left");var subQ2=sQuery(id+"F0.wireOp",EDGE,"E9");var subQ3=sQuery(id+"F0.wireOp",EDGE,"E20.right");var subQ4=sQuery(id+"F0.wireOp",EDGE,"E6");var subQ5=sQuery(id+"F0.wireOp",EDGE,"E7.top");var subQ6=sQuery(id+"F0.wireOp",EDGE,"E7.left");var subQ7=sQuery(id+"F0.wireOp",EDGE,"E28");var subQ8=sQuery(id+"F0.wireOp",EDGE,"E7.right");Q0=makeQuery(id+"F11.boolean.opBoolean","SPLIT",FACE,{"disambiguationData":[TD([makeQuery(id+"F1.opExtrude","SWEPT_FACE",FACE,{"disambiguationData":[OSD([subQ5])]})])],"derivedFrom":makeQuery(id+"F1.opExtrude","CAP_FACE",FACE,{"disambiguationData":[OSD([sQuery(id+"F0.wireOp",EDGE,"E0.top"),sQuery(id+"F0.wireOp",EDGE,"E1.left"),sQuery(id+"F0.wireOp",EDGE,"E1.right"),sQuery(id+"F0.wireOp",EDGE,"E4.top"),sQuery(id+"F0.wireOp",EDGE,"E5.right"),subQ4,subQ5,subQ6,subQ8,sQuery(id+"F0.wireOp",EDGE,"E8.left"),subQ2,sQuery(id+"F0.wireOp",EDGE,"E10.top"),sQuery(id+"F0.wireOp",EDGE,"E11"),sQuery(id+"F0.wireOp",EDGE,"E12"),sQuery(id+"F0.wireOp",EDGE,"E14"),sQuery(id+"F0.wireOp",EDGE,"E15"),sQuery(id+"F0.wireOp",EDGE,"E16"),sQuery(id+"F0.wireOp",EDGE,"E17"),sQuery(id+"F0.wireOp",EDGE,"E18"),sQuery(id+"F0.wireOp",EDGE,"E19"),sQuery(id+"F0.wireOp",EDGE,"E20.left"),subQ3,sQuery(id+"F0.wireOp",EDGE,"E21"),subQ1,sQuery(id+"F0.wireOp",EDGE,"E22.right"),sQuery(id+"F0.wireOp",EDGE,"E23"),sQuery(id+"F0.wireOp",EDGE,"E24"),subQ7,subQ0,sQuery(id+"F0.wireOp",EDGE,"E30.top"),sQuery(id+"F0.wireOp",EDGE,"E30.left"),sQuery(id+"F0.wireOp",EDGE,"E30.right")])],"isStart":false})});}
            extrude(context, id + "F34", {"entities" : qUnion([Q0]), "operationType" : NewBodyOperationType.REMOVE, "oppositeDirection" : true, "depth" : 3.17 * mm});
        }
        {
            var Q0;
            Q0=makeQuery(id+"F17.boolean.opBoolean","MERGE",FACE,{"derivedFrom":[makeQuery(id+"F13.boolean.opBoolean","MERGE",FACE,{"derivedFrom":[makeQuery(id+"F11.boolean.opBoolean","MERGE",FACE,{"derivedFrom":[makeQuery(id+"F1.opExtrude","SWEPT_FACE",FACE,{"disambiguationData":[OSD([sQuery(id+"F0.wireOp",EDGE,"E1.right")])]}),makeQuery(id+"F11.opExtrude","SWEPT_FACE",FACE,{"disambiguationData":[OSD([sQuery(id+"F10.wireOp",EDGE,"E72.right")])]})]}),makeQuery(id+"F13.opExtrude","SWEPT_FACE",FACE,{"disambiguationData":[OSD([sQuery(id+"F12.wireOp",EDGE,"E83.left")])]})]}),makeQuery(id+"F17.opExtrude","SWEPT_FACE",FACE,{"disambiguationData":[OSD([sQuery(id+"F16.wireOp",EDGE,"E114.right")])]}),makeQuery(id+"F17.opExtrude","SWEPT_FACE",FACE,{"disambiguationData":[OSD([sQuery(id+"F16.wireOp",EDGE,"E131.right")])]})]});
            var sketch = newSketch(context, id + "F35", { "sketchPlane" : qUnion([Q0])});
            skLineSegment(sketch, "E361.bottom", {"start": v(-28.58, 39.69) * mm, "end": v(-35.72, 39.69) * mm});
            skLineSegment(sketch, "E361.top", {"start": v(-28.58, 130.18) * mm, "end": v(-35.72, 130.18) * mm});
            skLineSegment(sketch, "E361.right", {"start": v(-35.72, 39.69) * mm, "end": v(-35.72, 130.18) * mm});
            skLineSegment(sketch, "E362", {"start": v(-28.58, 39.69) * mm, "end": v(-28.58, 73.03) * mm});
            skLineSegment(sketch, "E363", {"start": v(-28.57, 73.03) * mm, "end": v(-35.72, 80.17) * mm});
            skLineSegment(sketch, "E364", {"start": v(-28.58, 130.18) * mm, "end": v(-28.58, 96.84) * mm});
            skLineSegment(sketch, "E365", {"start": v(-28.57, 96.84) * mm, "end": v(-35.72, 89.7) * mm});
            skLineSegment(sketch, "E366", {"start": v(-28.58, 73.03) * mm, "end": v(-28.58, 96.84) * mm, "construction": true});
            skLineSegment(sketch, "E367", {"start": v(-28.58, 84.93) * mm, "end": v(-31.75, 84.93) * mm, "construction": true});
            skSolve(sketch);
        }
        {
            var Q0;
            Q0 = qSketchRegion(id + "F35", true);
            var Q1;
            Q1=makeQuery(id+"F17.boolean.opBoolean","MERGE",FACE,{"derivedFrom":[makeQuery(id+"F13.boolean.opBoolean","MERGE",FACE,{"derivedFrom":[makeQuery(id+"F11.boolean.opBoolean","MERGE",FACE,{"derivedFrom":[makeQuery(id+"F1.opExtrude","SWEPT_FACE",FACE,{"disambiguationData":[OSD([sQuery(id+"F0.wireOp",EDGE,"E11")])]}),makeQuery(id+"F11.opExtrude","SWEPT_FACE",FACE,{"disambiguationData":[OSD([sQuery(id+"F10.wireOp",EDGE,"E73.right")])]})]}),makeQuery(id+"F13.opExtrude","SWEPT_FACE",FACE,{"disambiguationData":[OSD([sQuery(id+"F12.wireOp",EDGE,"E83.right")])]})]}),makeQuery(id+"F17.opExtrude","SWEPT_FACE",FACE,{"disambiguationData":[OSD([sQuery(id+"F16.wireOp",EDGE,"E107.left")])]}),makeQuery(id+"F17.opExtrude","SWEPT_FACE",FACE,{"disambiguationData":[OSD([sQuery(id+"F16.wireOp",EDGE,"E135.left")])]})]});
            extrude(context, id + "F36", {"entities" : qUnion([Q0]), "operationType" : NewBodyOperationType.REMOVE, "endBound" : BoundingType.UP_TO_SURFACE, "oppositeDirection" : true, "endBoundEntityFace" : qUnion([Q1]), "depth" : 25.4 * mm});
        }
    });
